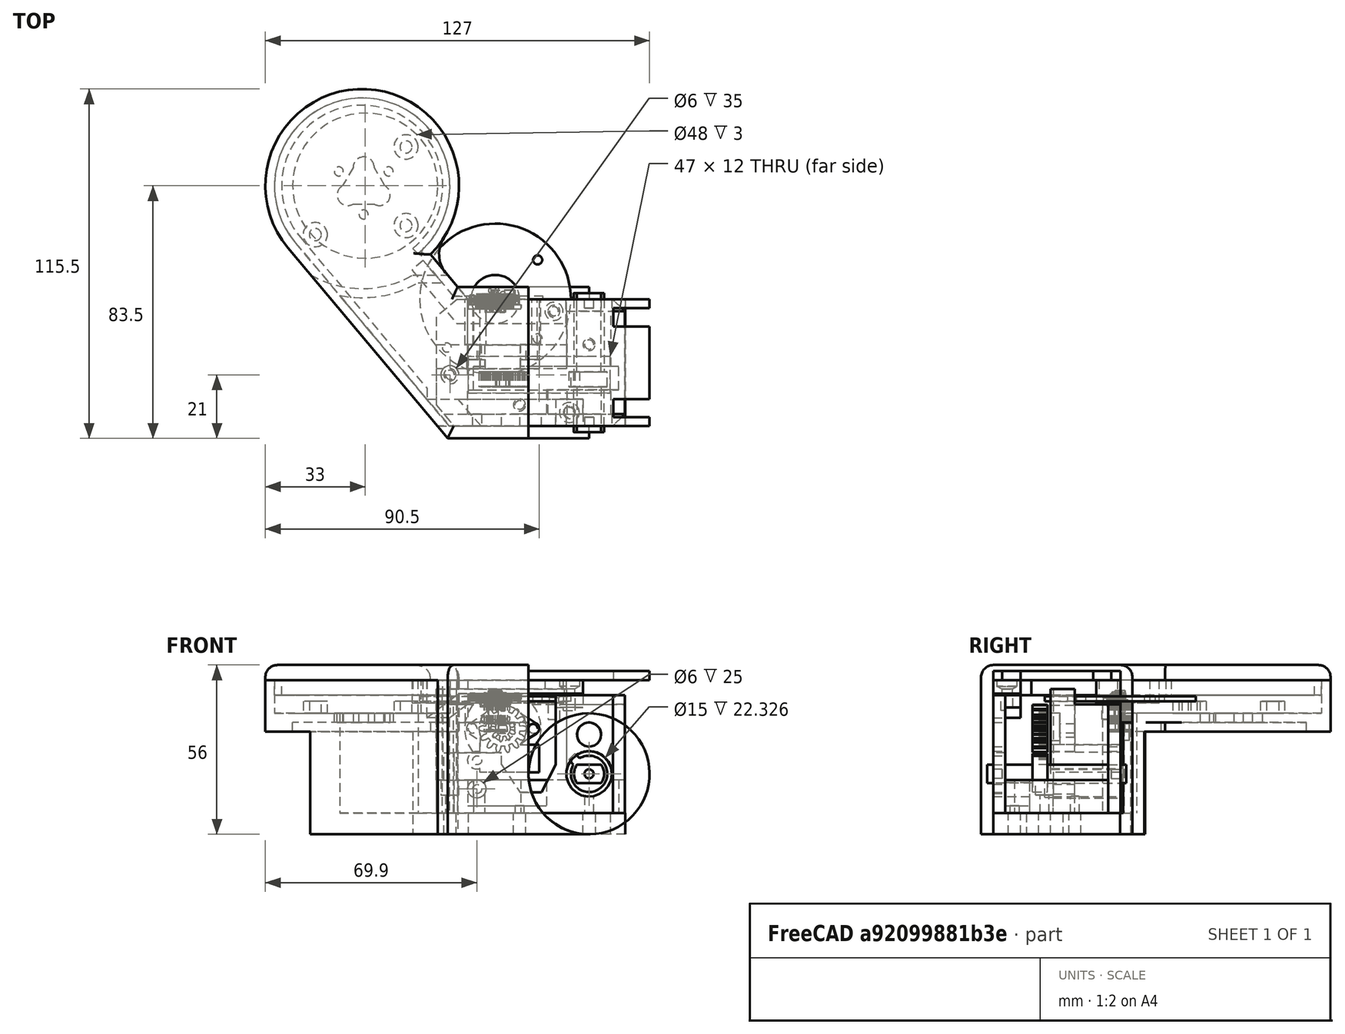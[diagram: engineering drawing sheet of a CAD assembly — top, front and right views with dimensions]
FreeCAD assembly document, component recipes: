
FREECAD ASSEMBLY — COMPONENT RECIPES ("ThirdArm")

This assembly document has 11 components, labeled P0..P10 below (a component is one placed body or linked part). 8 of them carry a construction recipe — the FreeCAD feature program that regenerates the part from scratch, quoted from this document or its linked companion documents; the rest are supplied as boundary geometry only. No exploded tour is included for this assembly.
COMPONENT P0 — recipe-attached ("SmallGear", modeled in this document).
Construction recipe (the document's own serialized feature program — sketch geometry with constraints, then the solid features built on it; lengths are millimeters unless a unit is written):

FEATURE [PartDesign::FeaturePython] InvoluteGear  label="InvoluteGear001"  # WARN: FeaturePython — macro-defined, semantics opaque (R4)
  AttacherType = Attacher::AttachEngine3D
  Suppressed = false
  addendum_diameter = 16
  angular_backlash = 0
  axle_hole = false
  axle_holesize = 10
  backlash = 0
  clearance = 0.25
  double_helix = false
  head = 0
  head_fillet = 0
  height = 5
  helix_angle = 0
  module = 1
  num_teeth = 14
  numpoints = 20
  offset_hole = false
  offset_holeoffset = 10
  offset_holesize = 10
  pitch_diameter = 14
  pressure_angle = 20
  properties_from_tool = false
  reversed_backlash = false
  root_diameter = 11.5
  root_fillet = 0
  shift = 0
  simple = false
  transverse_pitch = 3.14159
  traverse_module = 1
  undercut = false
  version = 1.3.0
  expr: angular_backlash = backlash / pitch_diameter * 360 ° / pi
FEATURE [Sketcher::SketchObject] Sketch002
  ArcFitTolerance = 1e-06
  AttachmentSupport = -> [InvoluteGear]
  FullyConstrained = false
  MakeInternals = false
  MapMode = 5
  Placement = pos=(0,0,5) rot=(0,0,1;0rad)
  sketch-geometry (5):
    g0: ArcOfCircle CenterX=0 CenterY=0 CenterZ=0 NormalX=0 NormalY=0 NormalZ=1 AngleXU=0 Radius=2.5 StartAngle=2.49809 EndAngle=3.78509
    g1: LineSegment StartX=2 StartY=1.5 StartZ=0 EndX=-2 EndY=1.5 EndZ=0
    g2: LineSegment StartX=-2 StartY=-1.5 StartZ=0 EndX=2 EndY=-1.5 EndZ=0
    g3: GeomPoint [constr] X=0 Y=0 Z=0
    g4: ArcOfCircle CenterX=0 CenterY=0 CenterZ=0 NormalX=0 NormalY=0 NormalZ=1 AngleXU=0 Radius=2.5 StartAngle=5.63968 EndAngle=6.92669
  constraints (10):
    c: Coincident(g0,g-1)
    c: Horizontal(g1)
    c: Horizontal(g2)
    c: Coincident(g3,g0)
    c: Equal(g0,g4)
    c: Coincident(g0,g4)
    c: Coincident(g2,g4)
    c: Coincident(g1,g4)
    c: Coincident(g1,g0)
    c: Coincident(g2,g0)
FEATURE [PartDesign::Pocket] Pocket001
  BaseFeature = -> InvoluteGear
  Direction = (0,0,-1)
  Length = 5
  Length2 = 5
  Profile = -> Sketch002
  ReferenceAxis = -> Sketch002 [N_Axis]
  Refine = true
  Suppressed = false
  Type = 1
FEATURE [PartDesign::Body] Body001  label="SmallGear"
  AllowCompound = false
  Group = -> [InvoluteGear,Sketch002,Pocket001]
  Origin = -> Origin002
  Placement = pos=(2.5,-24,-9) rot=(1,0,0;1.5708rad)
  Tip = -> Pocket001
COMPONENT P1 — recipe-attached ("ThirdArmHolder", modeled in this document).
Construction recipe (the document's own serialized feature program — sketch geometry with constraints, then the solid features built on it; lengths are millimeters unless a unit is written):

FEATURE [Sketcher::SketchObject] Sketch017
  ArcFitTolerance = 1e-06
  AttachmentSupport = -> [XY_Plane]
  FullyConstrained = false
  MakeInternals = false
  MapMode = 5
  sketch-geometry (4):
    g0: ArcOfCircle CenterX=-42 CenterY=37.5 CenterZ=0 NormalX=0 NormalY=0 NormalZ=1 AngleXU=0 Radius=32 StartAngle=5.49263 EndAngle=10.1229
    g1: LineSegment StartX=-66.5129 StartY=16.9302 StartZ=0 EndX=-6.82135 EndY=-54.2074 EndZ=0
    g2: LineSegment StartX=-19.4896 StartY=14.7562 StartZ=0 EndX=-6.82135 EndY=-0.341297 EndZ=0
    g3: LineSegment StartX=-6.82135 StartY=-0.341297 StartZ=0 EndX=-6.82135 EndY=-54.2074 EndZ=0
  constraints (10):
    c: Angle(g1,g-1) = 0.872665
    c: Angle(g-1,g2) = -0.872665
    c: Coincident(g3,g1)
    c: Vertical(g3)
    c: Coincident(g0,g1)
    c: Coincident(g0,g2)
    c: DistanceX(g0,g-1) = 42
    c: DistanceY(g-1,g0) = 37.5
    c: Radius(g0) = 32
    c: Coincident(g2,g3)
FEATURE [PartDesign::Pad] Pad010
  Direction = (0,0,1)
  Length = 14
  Length2 = 10
  Profile = -> Sketch017
  ReferenceAxis = -> Sketch017 [N_Axis]
  Refine = true
  Suppressed = false
  Type = 0
FEATURE [Sketcher::SketchObject] Sketch018
  ArcFitTolerance = 1e-06
  AttachmentSupport = -> [Pad010]
  ExternalGeometry = -> [Sketch017,Pad010]
  FullyConstrained = false
  MakeInternals = false
  MapMode = 5
  Placement = pos=(0,0,0) rot=(1,0,0;3.14159rad)
  sketch-geometry (8):
    g0: ArcOfCircle CenterX=-42 CenterY=-37.5 CenterZ=0 NormalX=0 NormalY=0 NormalZ=1 AngleXU=0 Radius=34 StartAngle=1.05435 EndAngle=2.09876
    g1: LineSegment StartX=-25.2111 StartY=-7.93429 StartZ=0 EndX=-13.7654 EndY=-7.93429 EndZ=0
    g2: LineSegment StartX=-13.7654 StartY=-7.93429 StartZ=0 EndX=-10.4314 EndY=-3.961 EndZ=0
    g3: LineSegment StartX=-59.1284 StartY=-8.12962 StartZ=0 EndX=-6.82135 EndY=54.2074 EndZ=0
    g4: GeomPoint X=-6.82135 Y=54.2074 Z=0
    g5: LineSegment StartX=-6.82135 StartY=54.2074 StartZ=0 EndX=45 EndY=54.2074 EndZ=0
    g6: LineSegment StartX=45 StartY=54.2074 StartZ=0 EndX=45 EndY=-3.961 EndZ=0
    g7: LineSegment StartX=45 StartY=-3.961 StartZ=0 EndX=-10.4314 EndY=-3.961 EndZ=0
  constraints (21):
    c: DistanceY(g0,g-1) = 37.5
    c: Coincident(g1,g0)
    c: Radius(g0) = 34
    c: Angle(g-1,g2) = 0.872665
    c: Coincident(g1,g2)
    c: Coincident(g0,g3)
    c: Angle(g-4) = 0.872665
    c: Angle(g-1,g3) = 0.872665
    c: Horizontal(g5)
    c: Coincident(g5,g3)
    c: Vertical(g6)
    c: Coincident(g6,g5)
    c: Horizontal(g7)
    c: Coincident(g3,g4)
    c: Coincident(g3,g-4)
    c: Coincident(g6,g7)
    c: Coincident(g2,g7)
    c: Horizontal(g1,g0)
    c: DistanceX(g0,g-1) = 42
    c: Block(g1)
    c: Distance(g-2,g6) = 45
FEATURE [PartDesign::Thickness] Thickness
  Base = -> Pad010 [Face6]
  BaseFeature = -> Pad010
  Intersection = true
  Join = 0
  Mode = 0
  Refine = true
  Reversed = true
  SupportTransform = false
  Suppressed = false
  Value = 3
FEATURE [PartDesign::Pad] Pad011
  BaseFeature = -> Thickness
  Direction = (0,0,-1)
  Length = 37
  Length2 = 10
  Profile = -> Sketch018
  ReferenceAxis = -> Sketch018 [N_Axis]
  Refine = true
  Suppressed = false
  Type = 0
FEATURE [Sketcher::SketchObject] Sketch019
  ArcFitTolerance = 1e-06
  AttachmentSupport = -> [Pad011]
  ExternalGeometry = -> [Pad011]
  FullyConstrained = false
  MakeInternals = false
  MapMode = 5
  Placement = pos=(0,0,14) rot=(0,0,1;0rad)
  sketch-geometry (10):
    g0: LineSegment StartX=-17.5 StartY=-62.76 StartZ=0 EndX=50.544 EndY=-62.76 EndZ=0
    g1: LineSegment StartX=50.544 StartY=-62.76 StartZ=0 EndX=50.544 EndY=0.961001 EndZ=0
    g2: LineSegment StartX=50.544 StartY=0.961001 StartZ=0 EndX=-17.0127 EndY=0.961001 EndZ=0
    g3: LineSegment StartX=-32.1829 StartY=-42 StartZ=0 EndX=-32.1829 EndY=-55.0243 EndZ=0
    g4: LineSegment StartX=-32.1829 StartY=-55.0243 StartZ=0 EndX=-17.5 EndY=-55.0243 EndZ=0
    g5: LineSegment StartX=-13.1484 StartY=-42 StartZ=0 EndX=-32.1829 EndY=-42 EndZ=0
    g6: LineSegment StartX=-17.5 StartY=-55.0243 StartZ=0 EndX=-17.5 EndY=-62.76 EndZ=0
    g7: LineSegment StartX=-19 StartY=-35.0263 StartZ=0 EndX=-13.1484 EndY=-42 EndZ=0
    g8: LineSegment StartX=-19 StartY=-35.0263 StartZ=0 EndX=-19 EndY=-1.02632 EndZ=0
    g9: LineSegment StartX=-19 StartY=-1.02632 StartZ=0 EndX=-17.0127 EndY=0.961001 EndZ=0
  constraints (24):
    c: Coincident(g0,g1)
    c: Coincident(g1,g2)
    c: Coincident(g6,g0)
    c: Horizontal(g0)
    c: Horizontal(g2)
    c: Vertical(g1)
    c: Distance(g-1,g0) = 62.76
    c: Coincident(g3,g4)
    c: Coincident(g5,g3)
    c: Vertical(g3)
    c: Horizontal(g4)
    c: Horizontal(g5)
    c: Coincident(g4,g6)
    c: Coincident(g7,g5)
    c: Distance(g-1,g5) = 42
    c: Coincident(g8,g7)
    c: Vertical(g8)
    c: Coincident(g9,g8)
    c: Coincident(g9,g2)
    c: Distance(g-2,g8) = 19
    c: Angle(g-1,g9) = 0.785398
    c: Angle(g7,g5) = 0.872665
    c: DistanceY(g8,g8) = 34
    c: Distance(g-4,g2) = 3
FEATURE [PartDesign::Pocket] Pocket007
  BaseFeature = -> Pad011
  Direction = (0,0,-1)
  Length = 44
  Length2 = 5
  Profile = -> Sketch019
  ReferenceAxis = -> Sketch019 [N_Axis]
  Refine = true
  Suppressed = false
  Type = 0
FEATURE [Sketcher::SketchObject] Sketch020
  ArcFitTolerance = 1e-06
  AttachmentSupport = -> [Pocket007]
  FullyConstrained = false
  MakeInternals = false
  MapMode = 5
  Placement = pos=(0,0,14) rot=(0,0,1;0rad)
  sketch-geometry (4):
    g0: LineSegment StartX=54.2024 StartY=-63.0343 StartZ=0 EndX=54.2024 EndY=-42 EndZ=0
    g1: LineSegment StartX=54.2024 StartY=-42 StartZ=0 EndX=-35.8003 EndY=-42 EndZ=0
    g2: LineSegment StartX=-35.8003 StartY=-42 StartZ=0 EndX=-35.8003 EndY=-63.0343 EndZ=0
    g3: LineSegment StartX=-35.8003 StartY=-63.0343 StartZ=0 EndX=54.2024 EndY=-63.0343 EndZ=0
  constraints (9):
    c: Coincident(g0,g1)
    c: Coincident(g1,g2)
    c: Coincident(g2,g3)
    c: Coincident(g3,g0)
    c: Vertical(g0)
    c: Vertical(g2)
    c: Horizontal(g1)
    c: Horizontal(g3)
    c: Distance(g-1,g1) = 42
FEATURE [PartDesign::Pocket] Pocket008
  BaseFeature = -> Pocket007
  Direction = (0,0,-1)
  Length = 5
  Length2 = 5
  Profile = -> Sketch020
  ReferenceAxis = -> Sketch020 [N_Axis]
  Refine = true
  Suppressed = false
  Type = 1
FEATURE [Sketcher::SketchObject] Sketch021
  ArcFitTolerance = 1e-06
  AttachmentSupport = -> [Pocket008]
  FullyConstrained = false
  MakeInternals = false
  MapMode = 5
  Placement = pos=(0,3.961,0) rot=(0,0.707107,0.707107;3.14159rad)
  sketch-geometry (5):
    g0: ArcOfCircle CenterX=-33 CenterY=-17 CenterZ=0 NormalX=0 NormalY=0 NormalZ=1 AngleXU=0 Radius=20 StartAngle=4.71239 EndAngle=6.28319
    g1: LineSegment StartX=-13 StartY=-17 StartZ=0 EndX=-13 EndY=6.96255 EndZ=0
    g2: LineSegment StartX=-13 StartY=6.96255 StartZ=0 EndX=-66.8614 EndY=6.96255 EndZ=0
    g3: LineSegment StartX=-66.8614 StartY=6.96255 StartZ=0 EndX=-66.8614 EndY=-37 EndZ=0
    g4: LineSegment StartX=-66.8614 StartY=-37 StartZ=0 EndX=-33.0001 EndY=-37 EndZ=0
  constraints (14):
    c: Radius(g0) = 20
    c: Distance(g0,g-1) = 17
    c: Vertical(g1)
    c: Coincident(g1,g0)
    c: Horizontal(g2)
    c: Coincident(g2,g1)
    c: Coincident(g0,g4)
    c: Coincident(g3,g4)
    c: Coincident(g2,g3)
    c: Horizontal(g0,g0)
    c: Horizontal(g4)
    c: Distance(g0,g-2) = 33
    c: Vertical(g3)
    c: Distance(g0,g4) = 20
FEATURE [PartDesign::Pocket] Pocket009
  BaseFeature = -> Pocket008
  Direction = (0,-1,2e-16)
  Length = 4
  Length2 = 5
  Profile = -> Sketch021
  ReferenceAxis = -> Sketch021 [N_Axis]
  Refine = true
  Suppressed = false
  Type = 0
FEATURE [Sketcher::SketchObject] Sketch031
  ArcFitTolerance = 1e-06
  AttachmentSupport = -> [Thickness]
  FullyConstrained = false
  MakeInternals = false
  MapMode = 5
  Placement = pos=(0,0,3) rot=(0,0,1;0rad)
  sketch-geometry (11):
    g0: GeomPoint [constr] X=-41.5 Y=37.5 Z=0
    g1: LineSegment StartX=-34.5 StartY=37.5 StartZ=0 EndX=-38 EndY=43.5622 EndZ=0
    g2: Circle [constr] CenterX=-41.5 CenterY=37.5 CenterZ=0 NormalX=0 NormalY=0 NormalZ=1 AngleXU=0 Radius=7
    g3: ArcOfCircle CenterX=-41.5 CenterY=43.5368 CenterZ=0 NormalX=0 NormalY=0 NormalZ=1 AngleXU=0 Radius=3.50009 StartAngle=0.00725319 EndAngle=3.13434
    g4: ArcOfCircle CenterX=-36.2363 CenterY=34.461 CenterZ=0 NormalX=0 NormalY=0 NormalZ=1 AngleXU=0 Radius=3.50004 StartAngle=4.18428 EndAngle=7.3349
    g5: ArcOfCircle CenterX=-46.7609 CenterY=34.4626 CenterZ=0 NormalX=0 NormalY=0 NormalZ=1 AngleXU=0 Radius=3.50002 StartAngle=2.0908 EndAngle=5.23958
    g6: LineSegment StartX=-45 StartY=43.5622 StartZ=0 EndX=-48.5 EndY=37.5 EndZ=0
    g7: LineSegment StartX=-45 StartY=31.4378 StartZ=0 EndX=-38 EndY=31.4378 EndZ=0
    g8: Circle CenterX=-41.5 CenterY=28 CenterZ=0 NormalX=0 NormalY=0 NormalZ=1 AngleXU=0 Radius=1.5
    g9: Circle CenterX=-33.2728 CenterY=42.25 CenterZ=0 NormalX=0 NormalY=0 NormalZ=1 AngleXU=0 Radius=1.5
    g10: Circle CenterX=-49.7272 CenterY=42.25 CenterZ=0 NormalX=0 NormalY=0 NormalZ=1 AngleXU=0 Radius=1.5
  constraints (24):
    c: DistanceX(g0,g-1) = 41.5
    c: DistanceY(g-1,g0) = 37.5
    c: PointOnObject(g1,g2)
    c: PointOnObject(g5,g2)
    c: PointOnObject(g4,g2)
    c: PointOnObject(g1,g2)
    c: Radius(g2) = 7
    c: Coincident(g2,g0)
    c: Coincident(g3,g1)
    c: Coincident(g4,g1)
    c: Coincident(g6,g3)
    c: Coincident(g6,g5)
    c: Coincident(g7,g5)
    c: Coincident(g7,g4)
    c: Horizontal(g7)
    c: Diameter(g8) = 3
    c: DistanceY(g8,g0) = 9.5
    c: Vertical(g0,g8)
    c: Diameter(g9) = 3
    c: Distance(g9,g0) = 9.5
    c: DistanceY(g0,g9) = 4.75
    c: Diameter(g10) = 3
    c: Distance(g10,g0) = 9.5
    c: DistanceY(g0,g10) = 4.75
FEATURE [PartDesign::Pocket] Pocket028
  BaseFeature = -> Pocket009
  Direction = (0,0,-1)
  Length = 5
  Length2 = 5
  Profile = -> Sketch031
  ReferenceAxis = -> Sketch031 [N_Axis]
  Refine = true
  Suppressed = false
  Type = 0
FEATURE [PartDesign::Fillet] Fillet006
  Base = -> Pocket028 [Edge1]
  BaseFeature = -> Pocket028
  Radius = 10
  Refine = true
  SupportTransform = false
  Suppressed = false
  UseAllEdges = false
FEATURE [Sketcher::SketchObject] Sketch052
  ArcFitTolerance = 1e-06
  FullyConstrained = false
  MakeInternals = false
  MapMode = 5
  Placement = pos=(0,0,0) rot=(1,0,0;3.14159rad)
  sketch-geometry (6):
    g0: ArcOfCircle CenterX=-42 CenterY=-37.5 CenterZ=0 NormalX=0 NormalY=0 NormalZ=1 AngleXU=0 Radius=32 StartAngle=2.44344 EndAngle=7.07374
    g1: ArcOfCircle CenterX=-42 CenterY=-37.5 CenterZ=0 NormalX=0 NormalY=0 NormalZ=1 AngleXU=0 Radius=34 StartAngle=1.05435 EndAngle=2.09876
    g2: LineSegment StartX=-59.1284 StartY=-8.12962 StartZ=0 EndX=-66.5129 EndY=-16.9302 EndZ=0
    g3: LineSegment StartX=-13.7654 StartY=-7.93429 StartZ=0 EndX=-25.2111 EndY=-7.93429 EndZ=0
    g4: LineSegment StartX=-13.7654 StartY=-7.93429 StartZ=0 EndX=-19.4896 EndY=-14.7562 EndZ=0
    g5: Circle CenterX=-41 CenterY=-37.5 CenterZ=0 NormalX=0 NormalY=0 NormalZ=1 AngleXU=0 Radius=24
  constraints (13):
    c: Coincident(g0,g-6)
    c: Coincident(g0,g-7)
    c: Coincident(g1,g0)
    c: Coincident(g1,g-6)
    c: Coincident(g2,g1)
    c: Coincident(g2,g0)
    c: Coincident(g3,g-5)
    c: Coincident(g3,g1)
    c: Coincident(g4,g3)
    c: Coincident(g4,g0)
    c: Diameter(g5) = 48
    c: Distance(g5,g-1) = 37.5
    c: Distance(g5,g-2) = 41
FEATURE [PartDesign::Pad] Pad021
  BaseFeature = -> Fillet006
  Direction = (0,-1e-16,-1)
  Length = 3
  Length2 = 10
  Profile = -> Sketch052
  ReferenceAxis = -> Sketch052 [N_Axis]
  Refine = true
  Suppressed = false
  Type = 0
FEATURE [Sketcher::SketchObject] Sketch053
  ArcFitTolerance = 1e-06
  AttachmentSupport = -> [Pocket028]
  ExternalGeometry = -> [Pocket028]
  FullyConstrained = false
  MakeInternals = false
  MapMode = 5
  Placement = pos=(0,0,3) rot=(0,0,1;0rad)
  sketch-geometry (7):
    g0: ArcOfCircle CenterX=-42 CenterY=37.5 CenterZ=0 NormalX=0 NormalY=0 NormalZ=1 AngleXU=0 Radius=37 StartAngle=4.50979 EndAngle=5.23479
    g1: LineSegment StartX=-23.5384 StartY=5.43491 StartZ=0 EndX=-15.5844 EndY=5.43491 EndZ=0
    g2: LineSegment StartX=-11.8303 StartY=0.961001 StartZ=0 EndX=-15.5844 EndY=5.43491 EndZ=0
    g3: LineSegment StartX=-11.8303 StartY=0.961001 StartZ=0 EndX=-17.0127 EndY=0.961001 EndZ=0
    g4: LineSegment StartX=-17.0127 StartY=0.961001 StartZ=0 EndX=-19 EndY=-1.0704 EndZ=0
    g5: LineSegment StartX=-19 StartY=-1.0704 StartZ=0 EndX=-19 EndY=-35.0263 EndZ=0
    g6: LineSegment StartX=-19 StartY=-35.0263 StartZ=0 EndX=-49.4452 EndY=1.2568 EndZ=0
  constraints (14):
    c: Radius(g0) = 37
    c: Horizontal(g1)
    c: Coincident(g1,g0)
    c: PointOnObject(g1,g-6)
    c: Coincident(g2,g-8)
    c: Coincident(g2,g1)
    c: Coincident(g3,g2)
    c: Coincident(g3,g-8)
    c: Coincident(g3,g4)
    c: Coincident(g4,g-9)
    c: Coincident(g4,g5)
    c: Coincident(g5,g-9)
    c: Coincident(g5,g6)
    c: Coincident(g6,g0)
FEATURE [PartDesign::Pocket] Pocket029
  BaseFeature = -> Pad021
  Direction = (0,0,-1)
  Length = 33
  Length2 = 5
  Profile = -> Sketch053
  ReferenceAxis = -> Sketch053 [N_Axis]
  Refine = true
  Suppressed = false
  Type = 0
FEATURE [Sketcher::SketchObject] Sketch054
  ArcFitTolerance = 1e-06
  AttachmentSupport = -> [Pocket029]
  FullyConstrained = true
  MakeInternals = false
  MapMode = 5
  Placement = pos=(0,0,-30) rot=(0,0,1;0rad)
  sketch-geometry (7):
    g0: Circle CenterX=-13 CenterY=-25 CenterZ=0 NormalX=0 NormalY=0 NormalZ=1 AngleXU=0 Radius=2
    g1: Circle CenterX=33 CenterY=-15 CenterZ=0 NormalX=0 NormalY=0 NormalZ=1 AngleXU=0 Radius=2
    g2: LineSegment StartX=-7 StartY=-19 StartZ=0 EndX=-7 EndY=-31 EndZ=0
    g3: LineSegment StartX=-7 StartY=-31 StartZ=0 EndX=40 EndY=-31 EndZ=0
    g4: LineSegment StartX=40 StartY=-31 StartZ=0 EndX=40 EndY=-19 EndZ=0
    g5: LineSegment StartX=40 StartY=-19 StartZ=0 EndX=-7 EndY=-19 EndZ=0
    g6: Circle CenterX=10 CenterY=-35 CenterZ=0 NormalX=0 NormalY=0 NormalZ=1 AngleXU=0 Radius=2
  constraints (21):
    c: Diameter(g0) = 4
    c: Diameter(g1) = 4
    c: DistanceY(g1,g-1) = 15
    c: Distance(g1,g-2) = 33
    c: DistanceX(g0,g-1) = 13
    c: DistanceY(g0,g-1) = 25
    c: Coincident(g2,g3)
    c: Coincident(g3,g4)
    c: Coincident(g4,g5)
    c: Coincident(g5,g2)
    c: Vertical(g2)
    c: Vertical(g4)
    c: Horizontal(g3)
    c: Horizontal(g5)
    c: DistanceY(g4,g4) = 12
    c: DistanceX(g3,g3) = 47
    c: DistanceY(g4,g-1) = 19
    c: DistanceX(g-1,g4) = 40
    c: Diameter(g6) = 4
    c: DistanceX(g-1,g6) = 10
    c: DistanceY(g6,g-1) = 35
FEATURE [PartDesign::Pocket] Pocket030
  BaseFeature = -> Pocket029
  Direction = (0,0,-1)
  Length = 5
  Length2 = 5
  Profile = -> Sketch054
  ReferenceAxis = -> Sketch054 [N_Axis]
  Refine = true
  Suppressed = false
  Type = 1
FEATURE [Sketcher::SketchObject] Sketch057
  ArcFitTolerance = 1e-06
  AttachmentSupport = -> [Pocket030]
  FullyConstrained = true
  MakeInternals = false
  MapMode = 5
  Placement = pos=(0,0.961001,0) rot=(1,0,0;1.5708rad)
  sketch-geometry (1):
    g0: Circle CenterX=4.5 CenterY=-2 CenterZ=0 NormalX=0 NormalY=0 NormalZ=1 AngleXU=0 Radius=4
  constraints (3):
    c: Diameter(g0) = 8
    c: DistanceX(g-1,g0) = 4.5
    c: DistanceY(g0,g-1) = 2
FEATURE [PartDesign::Pocket] Pocket033
  BaseFeature = -> Pocket030
  Direction = (0,1,-2e-16)
  Length = 2
  Length2 = 5
  Profile = -> Sketch057
  ReferenceAxis = -> Sketch057 [N_Axis]
  Refine = true
  Suppressed = false
  Type = 0
FEATURE [Sketcher::SketchObject] Sketch058
  ArcFitTolerance = 1e-06
  AttachmentSupport = -> [Pocket033]
  ExternalGeometry = -> [Pocket033]
  FullyConstrained = true
  MakeInternals = false
  MapMode = 5
  Placement = pos=(0,0,14) rot=(0,0,1;0rad)
  sketch-geometry (4):
    g0: LineSegment StartX=-13.1484 StartY=-42 StartZ=0 EndX=-20.7003 EndY=-33 EndZ=0
    g1: LineSegment StartX=-20.7003 StartY=-33 StartZ=0 EndX=31 EndY=-33 EndZ=0
    g2: LineSegment StartX=31 StartY=-33 StartZ=0 EndX=31 EndY=-42 EndZ=0
    g3: LineSegment StartX=31 StartY=-42 StartZ=0 EndX=-13.1484 EndY=-42 EndZ=0
  constraints (11):
    c: Coincident(g-3,g0)
    c: PointOnObject(g0,g-3)
    c: Coincident(g0,g1)
    c: Horizontal(g1)
    c: Coincident(g1,g2)
    c: Vertical(g2)
    c: Coincident(g2,g3)
    c: Coincident(g3,g0)
    c: Horizontal(g3)
    c: Distance(g-2,g2) = 31
    c: DistanceY(g2,g2) = 9
FEATURE [PartDesign::Pad] Pad022
  BaseFeature = -> Pocket033
  Direction = (0,0,1)
  Length = 4.5
  Length2 = 10
  Profile = -> Sketch058
  ReferenceAxis = -> Sketch058 [N_Axis]
  Refine = true
  Reversed = true
  Suppressed = false
  Type = 0
FEATURE [Sketcher::SketchObject] Sketch061
  ArcFitTolerance = 1e-06
  AttachmentSupport = -> [Pad022]
  FullyConstrained = true
  MakeInternals = false
  MapMode = 5
  Placement = pos=(0,0,14) rot=(0,0,1;0rad)
  sketch-geometry (1):
    g0: Circle CenterX=26.5 CenterY=-37.5 CenterZ=0 NormalX=0 NormalY=0 NormalZ=1 AngleXU=0 Radius=1.5
  constraints (3):
    c: Diameter(g0) = 3
    c: DistanceX(g-1,g0) = 26.5
    c: DistanceY(g0,g-1) = 37.5
FEATURE [PartDesign::Hole] Hole
  BaseFeature = -> Pad022
  CustomThreadClearance = 0
  Depth = 6
  DepthType = 0
  Diameter = 3.4
  DrillForDepth = false
  DrillPoint = 0
  DrillPointAngle = 118
  HoleCutCountersinkAngle = 90
  HoleCutCustomValues = false
  HoleCutDepth = 0
  HoleCutDiameter = 6.1
  HoleCutType = 0
  ModelThread = false
  Profile = -> Sketch061
  Refine = true
  Suppressed = false
  Tapered = false
  TaperedAngle = 90
  ThreadClass = 0
  ThreadDepth = 6
  ThreadDepthType = 0
  ThreadDirection = 0
  ThreadFit = 0
  ThreadSize = 9
  ThreadType = 1
  Threaded = false
  UseCustomThreadClearance = false
FEATURE [PartDesign::Hole] Hole001
  BaseFeature = -> Hole
  CustomThreadClearance = 0
  Depth = 2
  DepthType = 0
  Diameter = 6.6
  DrillForDepth = false
  DrillPoint = 1
  DrillPointAngle = 118
  HoleCutCountersinkAngle = 90
  HoleCutCustomValues = false
  HoleCutDepth = 0
  HoleCutDiameter = 0
  HoleCutType = 0
  ModelThread = false
  Profile = -> Sketch061
  Refine = true
  Suppressed = false
  Tapered = false
  TaperedAngle = 90
  ThreadClass = 0
  ThreadDepth = 2
  ThreadDepthType = 0
  ThreadDirection = 0
  ThreadFit = 0
  ThreadSize = 14
  ThreadType = 1
  Threaded = false
  UseCustomThreadClearance = false
FEATURE [PartDesign::Chamfer] Chamfer
  Angle = 45
  Base = -> Hole001 [Edge87]
  BaseFeature = -> Hole001
  ChamferType = 0
  FlipDirection = false
  Refine = true
  Size = 8
  Size2 = 1
  SupportTransform = false
  Suppressed = false
  UseAllEdges = false
FEATURE [Sketcher::SketchObject] Sketch062
  ArcFitTolerance = 1e-06
  AttachmentSupport = -> [Chamfer]
  ExternalGeometry = -> [Chamfer]
  FullyConstrained = false
  MakeInternals = false
  MapMode = 5
  Placement = pos=(0,0,14) rot=(0,0,1;0rad)
  sketch-geometry (8):
    g0: LineSegment StartX=-21.7877 StartY=12.8278 StartZ=0 EndX=-25.5719 EndY=9.6525 EndZ=0
    g1: LineSegment StartX=-25.5719 StartY=9.6525 StartZ=0 EndX=-10.7597 EndY=-8 EndZ=0
    g2: LineSegment StartX=-10.7597 StartY=-8 StartZ=0 EndX=25.4051 EndY=-8 EndZ=0
    g3: LineSegment StartX=25.4051 StartY=-8 StartZ=0 EndX=25.4051 EndY=0 EndZ=0
    g4: LineSegment StartX=-11.8303 StartY=0.961001 StartZ=0 EndX=-21.7877 EndY=12.8278 EndZ=0
    g5: LineSegment StartX=-11.8303 StartY=0.961001 StartZ=0 EndX=-7.9141 EndY=0.961001 EndZ=0
    g6: LineSegment StartX=-7.9141 StartY=0.961001 StartZ=0 EndX=-7.10773 EndY=1e-16 EndZ=0
    g7: LineSegment StartX=-7.10773 StartY=1e-16 StartZ=0 EndX=25.4051 EndY=1e-16 EndZ=0
  constraints (20):
    c: Coincident(g0,g1)
    c: Coincident(g1,g2)
    c: Horizontal(g2)
    c: Coincident(g2,g3)
    c: Coincident(g4,g0)
    c: Vertical(g3)
    c: Distance(g3,g3) = 8
    c: Angle(g4,g0) = 1.5708
    c: Angle(g1,g0) = 1.5708
    c: Coincident(g0,g-3)
    c: Angle(g4,g-1) = 0.872665
    c: PointOnObject(g4,g-4)
    c: Coincident(g4,g5)
    c: Coincident(g5,g-4)
    c: Coincident(g5,g6)
    c: PointOnObject(g6,g-1)
    c: Coincident(g6,g7)
    c: Coincident(g7,g3)
    c: Horizontal(g7)
    c: Angle(g7,g6) = 2.26893
FEATURE [PartDesign::Pad] Pad023
  BaseFeature = -> Chamfer
  Direction = (0,0,1)
  Length = 7.5
  Length2 = 10
  Profile = -> Sketch062
  ReferenceAxis = -> Sketch062 [N_Axis]
  Refine = true
  Reversed = true
  Suppressed = false
  Type = 0
FEATURE [Sketcher::SketchObject] Sketch063
  ArcFitTolerance = 1e-06
  AttachmentSupport = -> [Pad023]
  ExternalGeometry = -> [Pad023]
  FullyConstrained = true
  MakeInternals = false
  MapMode = 5
  Placement = pos=(0,0,14) rot=(0,0,1;0rad)
  sketch-geometry (1):
    g0: Circle CenterX=21.4051 CenterY=-4 CenterZ=0 NormalX=0 NormalY=0 NormalZ=1 AngleXU=0 Radius=1.5
  constraints (3):
    c: Diameter(g0) = 3
    c: Distance(g0,g-3) = 4
    c: DistanceY(g-3,g0) = 4
FEATURE [PartDesign::Hole] Hole002
  BaseFeature = -> Pad023
  CustomThreadClearance = 0
  Depth = 5
  DepthType = 0
  Diameter = 6
  DrillForDepth = false
  DrillPoint = 1
  DrillPointAngle = 118
  HoleCutCountersinkAngle = 90
  HoleCutCustomValues = false
  HoleCutDepth = 0
  HoleCutDiameter = 6.1
  HoleCutType = 0
  ModelThread = false
  Profile = -> Sketch063
  Refine = true
  Suppressed = false
  Tapered = false
  TaperedAngle = 90
  ThreadClass = 0
  ThreadDepth = 5
  ThreadDepthType = 0
  ThreadDirection = 0
  ThreadFit = 0
  ThreadSize = 0
  ThreadType = 0
  Threaded = false
  UseCustomThreadClearance = false
FEATURE [PartDesign::Pocket] Pocket035
  BaseFeature = -> Hole002
  Direction = (0,0,-1)
  Length = 8
  Length2 = 5
  Profile = -> Sketch063
  ReferenceAxis = -> Sketch063 [N_Axis]
  Refine = true
  Suppressed = false
  Type = 0
FEATURE [Sketcher::SketchObject] Sketch065
  ArcFitTolerance = 1e-06
  AttachmentSupport = -> [Pocket035]
  FullyConstrained = false
  MakeInternals = false
  MapMode = 5
  Placement = pos=(0,0,3) rot=(0,0,1;0rad)
  sketch-geometry (6):
    g0: Circle CenterX=-27.5 CenterY=50.3515 CenterZ=0 NormalX=0 NormalY=0 NormalZ=1 AngleXU=0 Radius=4
    g1: Circle CenterX=-27.5 CenterY=24.3515 CenterZ=0 NormalX=0 NormalY=0 NormalZ=1 AngleXU=0 Radius=4
    g2: Circle CenterX=-57.5 CenterY=21.3515 CenterZ=0 NormalX=0 NormalY=0 NormalZ=1 AngleXU=0 Radius=4
    g3: Circle CenterX=-27.5 CenterY=50.3515 CenterZ=0 NormalX=0 NormalY=0 NormalZ=1 AngleXU=0 Radius=2
    g4: Circle CenterX=-27.5 CenterY=24.3515 CenterZ=0 NormalX=0 NormalY=0 NormalZ=1 AngleXU=0 Radius=2
    g5: Circle CenterX=-57.5 CenterY=21.3515 CenterZ=0 NormalX=0 NormalY=0 NormalZ=1 AngleXU=0 Radius=2
  constraints (14):
    c: Diameter(g0) = 8
    c: Diameter(g1) = 8
    c: Vertical(g1,g0)
    c: DistanceX(g1,g-1) = 27.5
    c: Diameter(g2) = 8
    c: DistanceX(g2,g1) = 30
    c: DistanceY(g2,g1) = 3
    c: DistanceY(g1,g0) = 26
    c: Diameter(g3) = 4
    c: Coincident(g3,g0)
    c: Diameter(g4) = 4
    c: Coincident(g4,g1)
    c: Diameter(g5) = 4
    c: Coincident(g5,g2)
FEATURE [PartDesign::Pad] Pad024
  BaseFeature = -> Pocket035
  Direction = (0,0,1)
  Length = 4
  Length2 = 10
  Profile = -> Sketch065
  ReferenceAxis = -> Sketch065 [N_Axis]
  Refine = true
  Suppressed = false
  Type = 0
FEATURE [Sketcher::SketchObject] Sketch067
  ArcFitTolerance = 1e-06
  AttachmentSupport = -> [Pad024]
  ExternalGeometry = -> [Pad024]
  FullyConstrained = false
  MakeInternals = false
  MapMode = 5
  Placement = pos=(0,0,3) rot=(0,0,1;0rad)
  sketch-geometry (8):
    g0: LineSegment StartX=-41 StartY=37.5 StartZ=0 EndX=6.96769 EndY=-19.6657 EndZ=0
    g1: LineSegment StartX=6.96769 StartY=-42 StartZ=0 EndX=6.96769 EndY=0 EndZ=0
    g2: LineSegment StartX=6.96769 StartY=-19.6657 StartZ=0 EndX=33 EndY=-19.6657 EndZ=0
    g3: LineSegment StartX=33 StartY=-19.6657 StartZ=0 EndX=33 EndY=-16.3056 EndZ=0
    g4: LineSegment StartX=33 StartY=-16.3056 StartZ=0 EndX=29 EndY=-16.3056 EndZ=0
    g5: LineSegment StartX=33 StartY=-16.3056 StartZ=0 EndX=37 EndY=-16.3056 EndZ=0
    g6: LineSegment StartX=33 StartY=-19.6657 StartZ=0 EndX=153.063 EndY=-19.6657 EndZ=0
    g7: LineSegment StartX=153.063 StartY=-19.6657 StartZ=0 EndX=153.063 EndY=2.01091 EndZ=0
  constraints (20):
    c: Angle(g-1,g0) = -0.872665
    c: Coincident(g0,g-3)
    c: Symmetric(g-4,g-4,g1)
    c: PointOnObject(g1,g-5)
    c: Vertical(g1)
    c: PointOnObject(g0,g1)
    c: Coincident(g0,g2)
    c: Horizontal(g2)
    c: Vertical(g3)
    c: Coincident(g3,g2)
    c: Coincident(g3,g4)
    c: Coincident(g3,g5)
    c: Symmetric(g4,g5,g3)
    c: Horizontal(g4)
    c: DistanceX(g-1,g4) = 29
    c: DistanceX(g4,g5) = 8
    c: Coincident(g2,g6)
    c: Horizontal(g6)
    c: Coincident(g6,g7)
    c: Vertical(g7)
FEATURE [PartDesign::Body] Body004  label="ThirdArmHolder"
  AllowCompound = false
  Group = -> [Sketch017,Pad010,Thickness,Sketch018,Pad011,Sketch019,Pocket007,Sketch020,Pocket008,Sketch021,Pocket009,Sketch031,Pocket028,Fillet006,Sketch052,Pad021,Sketch053,Pocket029,Sketch054,Pocket030,Sketch057,Pocket033,Sketch058,Pad022,Sketch061,Hole,Hole001,Chamfer,Sketch062,Pad023,Sketch063,Hole002,Pocket035,Sketch065,Pad024,Sketch067]
  Origin = -> Origin
  Placement = pos=(-2,0,-7) rot=(0,0,1;0rad)
  Tip = -> Pad024
COMPONENT P2 — recipe-attached ("ThirdArmLid", modeled in this document).
Construction recipe (the document's own serialized feature program — sketch geometry with constraints, then the solid features built on it; lengths are millimeters unless a unit is written):

FEATURE [Sketcher::SketchObject] Sketch025
  ArcFitTolerance = 1e-06
  AttachmentSupport = -> [XY_Plane005]
  FullyConstrained = false
  MakeInternals = false
  MapMode = 5
  sketch-geometry (6):
    g0: ArcOfCircle CenterX=-42 CenterY=37.5 CenterZ=0 NormalX=0 NormalY=0 NormalZ=1 AngleXU=0 Radius=32 StartAngle=5.49278 EndAngle=10.1229
    g1: LineSegment StartX=-66.5134 StartY=16.9308 StartZ=0 EndX=-13.7082 EndY=-46 EndZ=0
    g2: LineSegment StartX=-19.4862 StartY=14.7596 StartZ=0 EndX=-10.4578 EndY=4 EndZ=0
    g3: LineSegment StartX=-13.7082 StartY=-46 StartZ=0 EndX=13 EndY=-46 EndZ=0
    g4: LineSegment StartX=-10.4578 StartY=4 StartZ=0 EndX=13 EndY=4 EndZ=0
    g5: LineSegment StartX=13 StartY=-46 StartZ=0 EndX=13 EndY=4 EndZ=0
  constraints (18):
    c: Angle(g1,g-1) = 0.872665
    c: Angle(g-1,g2) = -0.872665
    c: Coincident(g0,g1)
    c: Coincident(g0,g2)
    c: DistanceX(g0,g-1) = 42
    c: DistanceY(g-1,g0) = 37.5
    c: Radius(g0) = 32
    c: Distance(g-1,g2) = 5.44
    c: Horizontal(g3)
    c: Coincident(g3,g1)
    c: Horizontal(g4)
    c: Coincident(g4,g2)
    c: Vertical(g5)
    c: Coincident(g3,g5)
    c: Coincident(g4,g5)
    c: Distance(g-1,g3) = 46
    c: Distance(g-1,g4) = 4
    c: Distance(g-2,g5) = 13
FEATURE [PartDesign::Pad] Pad012  label="Pad00"
  Direction = (0,0,1)
  Length = 5
  Length2 = 10
  Profile = -> Sketch025
  ReferenceAxis = -> Sketch025 [N_Axis]
  Refine = true
  Suppressed = false
  Type = 0
FEATURE [Sketcher::SketchObject] Sketch026
  ArcFitTolerance = 1e-06
  AttachmentOffset = pos=(0,0,0) rot=(1,0,0;3.14159rad)
  AttachmentSupport = -> [Pad012]
  FullyConstrained = false
  MakeInternals = false
  MapMode = 5
  sketch-geometry (6):
    g0: ArcOfCircle CenterX=-42 CenterY=37.5 CenterZ=0 NormalX=0 NormalY=0 NormalZ=1 AngleXU=0 Radius=26.6323 StartAngle=5.39176 EndAngle=10.1229
    g1: LineSegment StartX=-62.4015 StartY=20.3811 StartZ=0 EndX=-20.5819 EndY=-29.4576 EndZ=0
    g2: ArcOfCircle CenterX=-42 CenterY=37.5 CenterZ=0 NormalX=0 NormalY=0 NormalZ=1 AngleXU=0 Radius=29 StartAngle=5.39774 EndAngle=10.1229
    g3: LineSegment StartX=-20.5819 StartY=-33.1411 StartZ=0 EndX=-64.2153 EndY=18.8592 EndZ=0
    g4: LineSegment StartX=-20.5819 StartY=-29.4576 StartZ=0 EndX=-20.5819 EndY=-33.1411 EndZ=0
    g5: LineSegment StartX=-23.6446 StartY=15.0483 StartZ=0 EndX=-25.2669 EndY=16.7809 EndZ=0
  constraints (13):
    c: Angle(g1,g-1) = 0.872665
    c: Coincident(g0,g1)
    c: DistanceX(g0,g-1) = 42
    c: DistanceY(g-1,g0) = 37.5
    c: Coincident(g2,g0)
    c: Diameter(g2) = 58
    c: Angle(g3,g-1) = 0.872665
    c: Coincident(g2,g3)
    c: Vertical(g1,g3)
    c: Coincident(g4,g1)
    c: Coincident(g4,g3)
    c: Coincident(g5,g2)
    c: Coincident(g0,g5)
FEATURE [PartDesign::Pad] Pad013
  BaseFeature = -> Pad012
  Direction = (0,1e-16,1)
  Length = 5
  Length2 = 10
  Profile = -> Sketch026
  ReferenceAxis = -> Sketch026 [N_Axis]
  Refine = true
  Reversed = true
  Suppressed = false
  Type = 0
FEATURE [Sketcher::SketchObject] Sketch027
  ArcFitTolerance = 1e-06
  AttachmentSupport = -> [Pad013]
  ExternalGeometry = -> [Pad013]
  FullyConstrained = false
  MakeInternals = false
  MapMode = 5
  Placement = pos=(0,0,0) rot=(1,0,0;3.14159rad)
  sketch-geometry (4):
    g0: LineSegment StartX=-10.4578 StartY=-4 StartZ=0 EndX=-7.10141 EndY=-4e-16 EndZ=0
    g1: LineSegment StartX=-7.10141 StartY=-4e-16 StartZ=0 EndX=13 EndY=-4e-16 EndZ=0
    g2: LineSegment StartX=13 StartY=-4e-16 StartZ=0 EndX=13 EndY=-4 EndZ=0
    g3: LineSegment StartX=13 StartY=-4 StartZ=0 EndX=-10.4578 EndY=-4 EndZ=0
  constraints (9):
    c: Coincident(g0,g1)
    c: Horizontal(g1)
    c: Coincident(g1,g2)
    c: Vertical(g2)
    c: Coincident(g2,g3)
    c: Coincident(g3,g0)
    c: Angle(g3,g0) = 0.872665
    c: Horizontal(g1,g-1)
    c: Coincident(g2,g-3)
FEATURE [PartDesign::Pad] Pad014
  BaseFeature = -> Pad013
  Direction = (0,0,-1)
  Length = 14
  Length2 = 10
  Profile = -> Sketch027
  ReferenceAxis = -> Sketch027 [N_Axis]
  Refine = true
  Suppressed = false
  Type = 0
FEATURE [Sketcher::SketchObject] Sketch028
  ArcFitTolerance = 1e-06
  AttachmentSupport = -> [Pad014]
  ExternalGeometry = -> [Pad014]
  FullyConstrained = true
  MakeInternals = false
  MapMode = 5
  Placement = pos=(0,0,0) rot=(1,0,0;3.14159rad)
  sketch-geometry (4):
    g0: LineSegment StartX=-13.7082 StartY=46 StartZ=0 EndX=-17.0646 EndY=42 EndZ=0
    g1: LineSegment StartX=-17.0646 StartY=42 StartZ=0 EndX=13 EndY=42 EndZ=0
    g2: LineSegment StartX=-13.7082 StartY=46 StartZ=0 EndX=13 EndY=46 EndZ=0
    g3: LineSegment StartX=13 StartY=42 StartZ=0 EndX=13 EndY=46 EndZ=0
  constraints (10):
    c: PointOnObject(g0,g-3)
    c: Coincident(g0,g1)
    c: Coincident(g0,g-3)
    c: Coincident(g2,g0)
    c: Coincident(g3,g1)
    c: Coincident(g3,g2)
    c: Vertical(g3)
    c: Distance(g-1,g1) = 42
    c: Horizontal(g1)
    c: Coincident(g3,g-4)
FEATURE [PartDesign::Pad] Pad015
  BaseFeature = -> Pad014
  Direction = (0,0,-1)
  Length = 51
  Length2 = 10
  Profile = -> Sketch028
  ReferenceAxis = -> Sketch028 [N_Axis]
  Refine = true
  Suppressed = false
  Type = 0
FEATURE [Sketcher::SketchObject] Sketch029
  ArcFitTolerance = 1e-06
  AttachmentSupport = -> [Pad015]
  FullyConstrained = true
  MakeInternals = false
  MapMode = 5
  Placement = pos=(0,-46,0) rot=(1,0,0;1.5708rad)
  sketch-geometry (3):
    g0: ArcOfCircle CenterX=33 CenterY=-31 CenterZ=0 NormalX=0 NormalY=0 NormalZ=1 AngleXU=0 Radius=20 StartAngle=3.14159 EndAngle=4.71239
    g1: LineSegment StartX=13 StartY=-31 StartZ=0 EndX=13 EndY=-51 EndZ=0
    g2: LineSegment StartX=13 StartY=-51 StartZ=0 EndX=33 EndY=-51 EndZ=0
  constraints (9):
    c: Horizontal(g0,g0)
    c: Radius(g0) = 20
    c: Coincident(g0,g1)
    c: DistanceY(g0,g-1) = 31
    c: Distance(g0,g-2) = 33
    c: Vertical(g1)
    c: DistanceY(g1,g1) = 20
    c: Coincident(g2,g1)
    c: Tangent(g2,g0) = -1.5708
FEATURE [PartDesign::Pad] Pad016
  BaseFeature = -> Pad015
  Direction = (0,-1,2e-16)
  Length = 4
  Length2 = 10
  Profile = -> Sketch029
  ReferenceAxis = -> Sketch029 [N_Axis]
  Refine = true
  Reversed = true
  Suppressed = false
  Type = 0
FEATURE [Sketcher::SketchObject] Sketch030
  ArcFitTolerance = 1e-06
  AttachmentSupport = -> [Pad016]
  FullyConstrained = true
  MakeInternals = false
  MapMode = 5
  Placement = pos=(13,0,0) rot=(0.57735,0.57735,0.57735;2.0944rad)
  sketch-geometry (4):
    g0: LineSegment StartX=-42 StartY=0 StartZ=0 EndX=0 EndY=0 EndZ=0
    g1: LineSegment StartX=-42 StartY=3 StartZ=0 EndX=-42 EndY=0 EndZ=0
    g2: LineSegment StartX=-42 StartY=3 StartZ=0 EndX=0 EndY=3 EndZ=0
    g3: LineSegment StartX=0 StartY=0 StartZ=0 EndX=0 EndY=3 EndZ=0
  constraints (11):
    c: Coincident(g1,g0)
    c: Coincident(g1,g2)
    c: PointOnObject(g2,g-2)
    c: Horizontal(g2)
    c: Coincident(g0,g3)
    c: Coincident(g3,g2)
    c: Vertical(g1)
    c: Horizontal(g0)
    c: Coincident(g0,g-1)
    c: DistanceY(g3,g3) = 3
    c: Distance(g-2,g1) = 42
FEATURE [PartDesign::Pad] Pad017
  BaseFeature = -> Pad016
  Direction = (1,0,0)
  Length = 40
  Length2 = 10
  Profile = -> Sketch030
  ReferenceAxis = -> Sketch030 [N_Axis]
  Refine = true
  Suppressed = false
  Type = 0
FEATURE [PartDesign::Fillet] Fillet003
  Base = -> Pad017 [Edge1]
  BaseFeature = -> Pad017
  Radius = 10
  Refine = true
  SupportTransform = false
  Suppressed = false
  UseAllEdges = false
FEATURE [PartDesign::Fillet] Fillet
  Base = -> Pad017 [Edge4,Edge7,Edge12,Edge13,Edge15]
  BaseFeature = -> Pad017
  Radius = 4
  Refine = true
  SupportTransform = false
  Suppressed = false
  UseAllEdges = false
FEATURE [Sketcher::SketchObject] Sketch066
  ArcFitTolerance = 1e-06
  AttachmentSupport = -> [Fillet]
  ExternalGeometry = -> [Fillet]
  FullyConstrained = true
  MakeInternals = false
  MapMode = 5
  Placement = pos=(0,0,3) rot=(0,0,1;0rad)
  sketch-geometry (8):
    g0: LineSegment StartX=53 StartY=-3 StartZ=0 EndX=41 EndY=-3 EndZ=0
    g1: LineSegment StartX=41 StartY=-3 StartZ=0 EndX=41 EndY=-9 EndZ=0
    g2: LineSegment StartX=41 StartY=-9 StartZ=0 EndX=53 EndY=-9 EndZ=0
    g3: LineSegment StartX=53 StartY=-9 StartZ=0 EndX=53 EndY=-3 EndZ=0
    g4: LineSegment StartX=53 StartY=-39 StartZ=0 EndX=53 EndY=-33 EndZ=0
    g5: LineSegment StartX=53 StartY=-33 StartZ=0 EndX=41 EndY=-33 EndZ=0
    g6: LineSegment StartX=41 StartY=-33 StartZ=0 EndX=41 EndY=-39 EndZ=0
    g7: LineSegment StartX=41 StartY=-39 StartZ=0 EndX=53 EndY=-39 EndZ=0
  constraints (24):
    c: Coincident(g0,g1)
    c: Coincident(g1,g2)
    c: Coincident(g2,g3)
    c: Coincident(g3,g0)
    c: Horizontal(g0)
    c: Horizontal(g2)
    c: Vertical(g1)
    c: Vertical(g3)
    c: PointOnObject(g0,g-3)
    c: Coincident(g4,g5)
    c: Coincident(g5,g6)
    c: Coincident(g6,g7)
    c: Coincident(g7,g4)
    c: Vertical(g4)
    c: Vertical(g6)
    c: Horizontal(g5)
    c: Horizontal(g7)
    c: PointOnObject(g4,g-3)
    c: Distance(g-1,g0) = 3
    c: DistanceY(g1,g1) = 6
    c: Distance(g-4,g7) = 3
    c: DistanceY(g6,g6) = 6
    c: DistanceX(g2,g2) = 12
    c: DistanceX(g5,g5) = 12
FEATURE [PartDesign::Pocket] Pocket037
  BaseFeature = -> Fillet
  Direction = (0,0,-1)
  Length = 5
  Length2 = 5
  Profile = -> Sketch066
  ReferenceAxis = -> Sketch066 [N_Axis]
  Refine = true
  Suppressed = false
  Type = 0
FEATURE [PartDesign::Body] Body005  label="ThirdArmLid"
  AllowCompound = false
  Group = -> [Pad012,Sketch025,Sketch026,Pad013,Sketch027,Pad014,Sketch028,Pad015,Sketch029,Pad016,Sketch030,Pad017,Fillet003,Fillet,Sketch066,Pocket037]
  Origin = -> Origin005
  Placement = pos=(-2,0,7) rot=(0,0,1;0rad)
  Tip = -> Pocket037
COMPONENT P3 — recipe-attached ("Bodyv2", modeled in this document).
Construction recipe (the document's own serialized feature program — sketch geometry with constraints, then the solid features built on it; lengths are millimeters unless a unit is written):

FEATURE [Sketcher::SketchObject] Sketch035
  ArcFitTolerance = 1e-06
  AttachmentSupport = -> [XZ_Plane007]
  FullyConstrained = true
  MakeInternals = false
  MapMode = 5
  Placement = pos=(0,0,0) rot=(1,0,0;1.5708rad)
  expr: Constraints[15] = <<Spreadsheet001>>.UpperLowerSpace
  expr: Constraints[7] = <<Spreadsheet001>>.CenterSpace
  sketch-geometry (6):
    g0: LineSegment StartX=42.83 StartY=-37 StartZ=0 EndX=42.83 EndY=4 EndZ=0
    g1: LineSegment StartX=42.83 StartY=4 StartZ=0 EndX=-19.5 EndY=4 EndZ=0
    g2: LineSegment StartX=-19.5 StartY=-37 StartZ=0 EndX=42.83 EndY=-37 EndZ=0
    g3: Circle CenterX=31 CenterY=-24 CenterZ=0 NormalX=0 NormalY=0 NormalZ=1 AngleXU=0 Radius=7.5
    g4: LineSegment StartX=-19.5 StartY=4 StartZ=0 EndX=-19.5 EndY=-37 EndZ=0
    g5: Circle CenterX=31 CenterY=-11 CenterZ=0 NormalX=0 NormalY=0 NormalZ=1 AngleXU=0 Radius=4
  constraints (18):
    c: Coincident(g0,g1)
    c: Vertical(g0)
    c: Horizontal(g1)
    c: Horizontal(g2)
    c: Coincident(g4,g2)
    c: Vertical(g4)
    c: Coincident(g0,g2)
    c: Distance(g3,g-2) = 31
    c: Diameter(g3) = 15
    c: Diameter(g5) = 8
    c: Vertical(g3,g5)
    c: Distance(g-1,g1) = 4
    c: Distance(g-1,g2) = 37
    c: Distance(g0,g-2) = 42.83
    c: Distance(g3,g2) = 13
    c: DistanceY(g3,g5) = 13
    c: Coincident(g1,g4)
    c: Distance(g-2,g4) = 19.5
FEATURE [PartDesign::Pad] Pad019
  Direction = (0,-1,2e-16)
  Length = 42
  Length2 = 10
  Placement = pos=(0,0,0) rot=(1,0,0;1.5708rad)
  Profile = -> Sketch035
  ReferenceAxis = -> Sketch035 [N_Axis]
  Refine = true
  Suppressed = false
  Type = 0
FEATURE [Sketcher::SketchObject] Sketch036
  ArcFitTolerance = 1e-06
  AttachmentSupport = -> [Pad019]
  ExternalGeometry = -> [Pad019]
  FullyConstrained = false
  MakeInternals = false
  MapMode = 5
  Placement = pos=(0,1.8e-15,4) rot=(0,0,1;3.14159rad)
  sketch-geometry (7):
    g0: LineSegment StartX=-50.4105 StartY=38 StartZ=0 EndX=-50.4105 EndY=18.9532 EndZ=0
    g1: LineSegment StartX=41.4002 StartY=23 StartZ=0 EndX=41.4002 EndY=38 EndZ=0
    g2: LineSegment StartX=41.4002 StartY=38 StartZ=0 EndX=-50.4105 EndY=38 EndZ=0
    g3: LineSegment StartX=-50.4105 StartY=18.9532 StartZ=0 EndX=-50.4105 EndY=4 EndZ=0
    g4: LineSegment StartX=-50.4105 StartY=4 StartZ=0 EndX=-23.5 EndY=4 EndZ=0
    g5: LineSegment StartX=-23.5 StartY=4 StartZ=0 EndX=-23.5 EndY=23 EndZ=0
    g6: LineSegment StartX=-23.5 StartY=23 StartZ=0 EndX=41.4002 EndY=23 EndZ=0
  constraints (18):
    c: Coincident(g1,g2)
    c: Coincident(g2,g0)
    c: Vertical(g0)
    c: Vertical(g1)
    c: Horizontal(g2)
    c: Coincident(g3,g4)
    c: Coincident(g4,g5)
    c: Vertical(g3)
    c: Vertical(g5)
    c: Horizontal(g4)
    c: Coincident(g3,g0)
    c: Coincident(g6,g5)
    c: Coincident(g6,g1)
    c: Horizontal(g6)
    c: Distance(g-1,g4) = 4
    c: Distance(g-2,g5) = 23.5
    c: Distance(g-3,g2) = 4
    c: Distance(g-1,g6) = 23
FEATURE [PartDesign::Pocket] Pocket015
  BaseFeature = -> Pad019
  Direction = (0,0,-1)
  Length = 30
  Length2 = 5
  Placement = pos=(0,0,0) rot=(1,0,0;1.5708rad)
  Profile = -> Sketch036
  ReferenceAxis = -> Sketch036 [N_Axis]
  Refine = true
  Suppressed = false
  Type = 0
FEATURE [Sketcher::SketchObject] Sketch037
  ArcFitTolerance = 1e-06
  AttachmentSupport = -> [Pocket015]
  ExternalGeometry = -> [Pocket015]
  FullyConstrained = false
  MakeInternals = false
  MapMode = 5
  Placement = pos=(0,0,-26) rot=(0,0,1;3.14159rad)
  sketch-geometry (15):
    g0: LineSegment StartX=-40.79 StartY=30.0707 StartZ=0 EndX=-40.79 EndY=22.3263 EndZ=0
    g1: LineSegment StartX=-40.79 StartY=22.3263 StartZ=0 EndX=-8.42993 EndY=22.3263 EndZ=0
    g2: Circle CenterX=-31 CenterY=15 CenterZ=0 NormalX=0 NormalY=0 NormalZ=1 AngleXU=0 Radius=1.5
    g3: Circle CenterX=15 CenterY=25 CenterZ=0 NormalX=0 NormalY=0 NormalZ=1 AngleXU=0 Radius=1.5
    g4: Circle CenterX=0 CenterY=35 CenterZ=0 NormalX=0 NormalY=0 NormalZ=1 AngleXU=0 Radius=1.5
    g5: LineSegment StartX=-8.42993 StartY=22.3263 StartZ=0 EndX=-8.42993 EndY=15.2343 EndZ=0
    g6: LineSegment StartX=-8.42993 StartY=15.2343 StartZ=0 EndX=3.56508 EndY=15.2343 EndZ=0
    g7: LineSegment StartX=3.56508 StartY=15.2343 StartZ=0 EndX=3.56508 EndY=22.3263 EndZ=0
    g8: LineSegment StartX=3.56508 StartY=22.3263 StartZ=0 EndX=7.24123 EndY=22.3263 EndZ=0
    g9: LineSegment StartX=-16.9534 StartY=30.0707 StartZ=0 EndX=-16.9534 EndY=38 EndZ=0
    g10: LineSegment StartX=-40.79 StartY=30.0707 StartZ=0 EndX=-16.9534 EndY=30.0707 EndZ=0
    g11: LineSegment StartX=-16.9534 StartY=38 StartZ=0 EndX=9.08031 EndY=38 EndZ=0
    g12: LineSegment StartX=9.08031 StartY=38 StartZ=0 EndX=9.08031 EndY=30.0707 EndZ=0
    g13: LineSegment StartX=9.08031 StartY=30.0707 StartZ=0 EndX=7.24123 EndY=30.0707 EndZ=0
    g14: LineSegment StartX=7.24123 StartY=30.0707 StartZ=0 EndX=7.24123 EndY=22.3263 EndZ=0
  constraints (34):
    c: Coincident(g0,g1)
    c: Vertical(g0)
    c: Horizontal(g1)
    c: Diameter(g2) = 3
    c: Distance(g2,g-1) = 15
    c: Diameter(g3) = 3
    c: PointOnObject(g4,g-2)
    c: Diameter(g4) = 3
    c: DistanceY(g-1,g3) = 25
    c: DistanceY(g-1,g4) = 35
    c: Distance(g3,g-2) = 15
    c: Coincident(g5,g6)
    c: Coincident(g6,g7)
    c: Vertical(g5)
    c: Vertical(g7)
    c: Horizontal(g6)
    c: Coincident(g5,g1)
    c: Coincident(g7,g8)
    c: DistanceX(g2,g-1) = 31
    c: Vertical(g9)
    c: Coincident(g0,g10)
    c: Coincident(g10,g9)
    c: Horizontal(g10)
    c: Horizontal(g11)
    c: Coincident(g11,g12)
    c: Vertical(g12)
    c: Coincident(g12,g13)
    c: Horizontal(g13)
    c: Coincident(g13,g14)
    c: Coincident(g14,g8)
    c: Vertical(g14)
    c: Coincident(g9,g11)
    c: Horizontal(g9,g13)
    c: Horizontal(g11,g-3)
FEATURE [PartDesign::Pocket] Pocket016
  BaseFeature = -> Pocket015
  Direction = (0,0,-1)
  Length = 5
  Length2 = 5
  Placement = pos=(0,0,0) rot=(1,0,0;1.5708rad)
  Profile = -> Sketch037
  ReferenceAxis = -> Sketch037 [N_Axis]
  Refine = true
  Suppressed = false
  Type = 1
FEATURE [Sketcher::SketchObject] Sketch038
  ArcFitTolerance = 1e-06
  AttachmentSupport = -> [Pocket016]
  FullyConstrained = false
  MakeInternals = false
  MapMode = 5
  Placement = pos=(0,-42,0) rot=(1,0,0;1.5708rad)
  sketch-geometry (8):
    g0: LineSegment StartX=20 StartY=-21 StartZ=0 EndX=20 EndY=12.6879 EndZ=0
    g1: LineSegment StartX=20 StartY=12.6879 StartZ=0 EndX=-22.1888 EndY=12.6879 EndZ=0
    g2: LineSegment StartX=2.00581 StartY=-21 StartZ=0 EndX=8.1848 EndY=-30.0757 EndZ=0
    g3: LineSegment StartX=8.1848 StartY=-30.0757 StartZ=0 EndX=15.2981 EndY=-30.0757 EndZ=0
    g4: LineSegment StartX=15.2981 StartY=-30.0757 StartZ=0 EndX=20 EndY=-21 EndZ=0
    g5: LineSegment StartX=2.00581 StartY=-21 StartZ=0 EndX=2.00581 EndY=-17 EndZ=0
    g6: LineSegment StartX=2.00581 StartY=-17 StartZ=0 EndX=-22.1888 EndY=-17 EndZ=0
    g7: LineSegment StartX=-22.1888 StartY=-17 StartZ=0 EndX=-22.1888 EndY=12.6879 EndZ=0
  constraints (17):
    c: Coincident(g0,g1)
    c: Vertical(g0)
    c: Horizontal(g1)
    c: Distance(g-2,g0) = 20
    c: Coincident(g2,g3)
    c: Horizontal(g3)
    c: Coincident(g3,g4)
    c: Horizontal(g0,g2)
    c: Coincident(g0,g4)
    c: Coincident(g2,g5)
    c: Vertical(g5)
    c: Coincident(g5,g6)
    c: Coincident(g6,g7)
    c: Vertical(g7)
    c: Coincident(g1,g7)
    c: Horizontal(g6)
    c: Distance(g-3,g6) = 20
FEATURE [PartDesign::Pocket] Pocket017
  BaseFeature = -> Pocket016
  Direction = (0,1,-2e-16)
  Length = 15
  Length2 = 5
  Placement = pos=(0,0,0) rot=(1,0,0;1.5708rad)
  Profile = -> Sketch038
  ReferenceAxis = -> Sketch038 [N_Axis]
  Refine = true
  Suppressed = false
  Type = 0
FEATURE [Sketcher::SketchObject] Sketch039
  ArcFitTolerance = 1e-06
  AttachmentSupport = -> [Pocket017]
  FullyConstrained = true
  MakeInternals = false
  MapMode = 5
  Placement = pos=(0,-23,5.1e-15) rot=(1,0,0;1.5708rad)
  sketch-geometry (2):
    g0: Circle CenterX=-7.5 CenterY=-9 CenterZ=0 NormalX=0 NormalY=0 NormalZ=1 AngleXU=0 Radius=1.5
    g1: Circle CenterX=12.5 CenterY=-9 CenterZ=0 NormalX=0 NormalY=0 NormalZ=1 AngleXU=0 Radius=1.5
  constraints (6):
    c: Diameter(g0) = 3
    c: DistanceX(g0,g-1) = 7.5
    c: Diameter(g1) = 3
    c: DistanceX(g0,g1) = 20
    c: Horizontal(g0,g1)
    c: DistanceY(g0,g-1) = 9
FEATURE [PartDesign::Pocket] Pocket018
  BaseFeature = -> Pocket017
  Direction = (0,1,-2e-16)
  Length = 10
  Length2 = 5
  Placement = pos=(0,0,0) rot=(1,0,0;1.5708rad)
  Profile = -> Sketch039
  ReferenceAxis = -> Sketch039 [N_Axis]
  Refine = true
  Suppressed = false
  Type = 0
FEATURE [Sketcher::SketchObject] Sketch040
  ArcFitTolerance = 1e-06
  AttachmentSupport = -> [Pocket018]
  ExternalGeometry = -> [Pocket018]
  FullyConstrained = true
  MakeInternals = false
  MapMode = 5
  Placement = pos=(0,-1.63e-14,-37) rot=(1,0,0;3.14159rad)
  sketch-geometry (4):
    g0: LineSegment StartX=-9.08031 StartY=38 StartZ=0 EndX=-9.08031 EndY=30.0707 EndZ=0
    g1: LineSegment StartX=-9.08031 StartY=30.0707 StartZ=0 EndX=16.9534 EndY=30.0707 EndZ=0
    g2: LineSegment StartX=-9.08031 StartY=38 StartZ=0 EndX=16.9534 EndY=38 EndZ=0
    g3: LineSegment StartX=16.9534 StartY=38 StartZ=0 EndX=16.9534 EndY=30.0707 EndZ=0
  constraints (9):
    c: Vertical(g0)
    c: Coincident(g0,g1)
    c: Coincident(g0,g-5)
    c: Coincident(g1,g-4)
    c: Coincident(g0,g2)
    c: Coincident(g2,g-4)
    c: Horizontal(g2)
    c: Coincident(g2,g3)
    c: Coincident(g3,g1)
FEATURE [PartDesign::Pad] Pad020
  BaseFeature = -> Pocket018
  Direction = (0,0,-1)
  Length = 2.5
  Length2 = 10
  Placement = pos=(0,0,0) rot=(1,0,0;1.5708rad)
  Profile = -> Sketch040
  ReferenceAxis = -> Sketch040 [N_Axis]
  Refine = true
  Reversed = true
  Suppressed = false
  Type = 0
FEATURE [Sketcher::SketchObject] Sketch041
  ArcFitTolerance = 1e-06
  AttachmentSupport = -> [Pad020]
  FullyConstrained = true
  MakeInternals = false
  MapMode = 5
  Placement = pos=(0,-38,0) rot=(-1,0,0;1.5708rad)
  sketch-geometry (2):
    g0: Circle CenterX=-6 CenterY=29 CenterZ=0 NormalX=0 NormalY=0 NormalZ=1 AngleXU=0 Radius=1.5
    g1: Circle CenterX=-6 CenterY=19.5 CenterZ=0 NormalX=0 NormalY=0 NormalZ=1 AngleXU=0 Radius=1.5
  constraints (6):
    c: Diameter(g0) = 3
    c: Diameter(g1) = 3
    c: DistanceY(g-1,g1) = 19.5
    c: DistanceY(g1,g0) = 9.5
    c: Vertical(g0,g1)
    c: Distance(g1,g-2) = 6
FEATURE [PartDesign::Pocket] Pocket019
  BaseFeature = -> Pad020
  Direction = (0,-1,-2e-16)
  Length = 5
  Length2 = 5
  Placement = pos=(0,0,0) rot=(1,0,0;1.5708rad)
  Profile = -> Sketch041
  ReferenceAxis = -> Sketch041 [N_Axis]
  Refine = true
  Suppressed = false
  Type = 1
FEATURE [Sketcher::SketchObject] Sketch042
  ArcFitTolerance = 1e-06
  AttachmentSupport = -> [Pocket019]
  FullyConstrained = false
  MakeInternals = false
  MapMode = 5
  Placement = pos=(0,-3.8e-15,0) rot=(-1,0,0;1.5708rad)
  sketch-geometry (6):
    g0: ArcOfCircle CenterX=2.5 CenterY=9 CenterZ=0 NormalX=0 NormalY=0 NormalZ=1 AngleXU=0 Radius=7.75 StartAngle=2.74605 EndAngle=7.03661
    g1: LineSegment StartX=-5 StartY=23.565 StartZ=0 EndX=-5 EndY=11.9862 EndZ=0
    g2: LineSegment StartX=-5 StartY=11.9862 StartZ=0 EndX=-4.6516 EndY=11.9862 EndZ=0
    g3: LineSegment StartX=14.5 StartY=14.3021 StartZ=0 EndX=14.5 EndY=23.565 EndZ=0
    g4: LineSegment StartX=14.5 StartY=23.565 StartZ=0 EndX=-5 EndY=23.565 EndZ=0
    g5: LineSegment StartX=8.15247 StartY=14.3021 StartZ=0 EndX=14.5 EndY=14.3021 EndZ=0
  constraints (16):
    c: DistanceX(g-1,g0) = 2.5
    c: DistanceY(g-1,g0) = 9
    c: Diameter(g0) = 15.5
    c: Coincident(g1,g2)
    c: Coincident(g5,g3)
    c: Coincident(g3,g4)
    c: Coincident(g4,g1)
    c: Vertical(g1)
    c: Vertical(g3)
    c: Horizontal(g2)
    c: Horizontal(g4)
    c: Distance(g0,g1) = 7.5
    c: Distance(g0,g3) = 12
    c: Coincident(g0,g5)
    c: Coincident(g0,g2)
    c: Horizontal(g5)
FEATURE [PartDesign::Pocket] Pocket020
  BaseFeature = -> Pocket019
  Direction = (0,-1,-2e-16)
  Length = 35
  Length2 = 5
  Placement = pos=(0,0,0) rot=(1,0,0;1.5708rad)
  Profile = -> Sketch042
  ReferenceAxis = -> Sketch042 [N_Axis]
  Refine = true
  Suppressed = false
  Type = 0
FEATURE [Sketcher::SketchObject] Sketch044
  ArcFitTolerance = 1e-06
  AttachmentSupport = -> [Pocket020]
  FullyConstrained = true
  MakeInternals = false
  MapMode = 5
  Placement = pos=(0,-2.52e-14,-37) rot=(1,0,0;3.14159rad)
  sketch-geometry (1):
    g0: Circle CenterX=8 CenterY=35 CenterZ=0 NormalX=0 NormalY=0 NormalZ=1 AngleXU=0 Radius=1.5
  constraints (3):
    c: Diameter(g0) = 3
    c: Distance(g0,g-2) = 8
    c: DistanceY(g-1,g0) = 35
FEATURE [PartDesign::Pocket] Pocket022
  BaseFeature = -> Pocket020
  Direction = (0,0,1)
  Length = 5
  Length2 = 5
  Placement = pos=(0,0,0) rot=(1,0,0;1.5708rad)
  Profile = -> Sketch044
  ReferenceAxis = -> Sketch044 [N_Axis]
  Refine = true
  Suppressed = false
  Type = 0
FEATURE [PartDesign::Chamfer] Chamfer002
  Angle = 45
  Base = -> Pocket022 [Edge7,Edge1]
  BaseFeature = -> Pocket022
  ChamferType = 0
  FlipDirection = false
  Placement = pos=(0,0,0) rot=(1,0,0;1.5708rad)
  Refine = true
  Size = 4
  Size2 = 1
  SupportTransform = false
  Suppressed = false
  UseAllEdges = false
FEATURE [Sketcher::SketchObject] Sketch045
  ArcFitTolerance = 1e-06
  AttachmentSupport = -> [Chamfer002]
  FullyConstrained = false
  MakeInternals = false
  MapMode = 5
  Placement = pos=(0,-23,5.1e-15) rot=(1,0,0;1.5708rad)
  sketch-geometry (8):
    g0: ArcOfCircle CenterX=2.5 CenterY=-9 CenterZ=0 NormalX=0 NormalY=0 NormalZ=1 AngleXU=0 Radius=7.5 StartAngle=4.12969 EndAngle=5.2949
    g1: ArcOfCircle CenterX=12.5 CenterY=-9 CenterZ=0 NormalX=0 NormalY=0 NormalZ=1 AngleXU=0 Radius=2 StartAngle=5.29475 EndAngle=7.27178
    g2: LineSegment StartX=-8.59969 StartY=-7.3276 StartZ=0 EndX=-1.62383 EndY=-2.7355 EndZ=0
    g3: LineSegment StartX=-8.60796 StartY=-10.6632 StartZ=0 EndX=-1.62713 EndY=-15.2623 EndZ=0
    g4: LineSegment StartX=6.625 StartY=-2.73627 StartZ=0 EndX=13.5997 EndY=-7.32949 EndZ=0
    g5: LineSegment StartX=13.6 StartY=-10.6703 StartZ=0 EndX=6.62595 EndY=-15.2631 EndZ=0
    g6: ArcOfCircle CenterX=2.5 CenterY=-9 CenterZ=0 NormalX=0 NormalY=0 NormalZ=1 AngleXU=0 Radius=7.5 StartAngle=0.988432 EndAngle=2.15297
    g7: ArcOfCircle CenterX=-7.5 CenterY=-8.99814 CenterZ=0 NormalX=0 NormalY=0 NormalZ=1 AngleXU=0 Radius=2 StartAngle=2.15297 EndAngle=4.12525
  constraints (21):
    c: Distance(g0,g-1) = 9
    c: DistanceX(g-1,g0) = 2.5
    c: DistanceX(g0,g1) = 10
    c: Horizontal(g0,g1)
    c: Distance(g0,g2) = 7.5
    c: Distance(g0,g3) = 7.5
    c: Distance(g0,g4) = 7.5
    c: Distance(g1,g4) = 2
    c: Distance(g0,g5) = 7.5
    c: Coincident(g0,g5)
    c: Coincident(g1,g4)
    c: Coincident(g1,g5)
    c: Coincident(g6,g0)
    c: Coincident(g6,g2)
    c: Coincident(g6,g4)
    c: Radius(g7) = 2
    c: Coincident(g7,g2)
    c: Coincident(g7,g3)
    c: DistanceX(g7,g0) = 10
    c: Distance(g7,g2) = 2
    c: Coincident(g0,g3)
FEATURE [PartDesign::Pocket] Pocket023
  BaseFeature = -> Chamfer002
  Direction = (0,1,-2e-16)
  Length = 3
  Length2 = 5
  Placement = pos=(0,0,0) rot=(1,0,0;1.5708rad)
  Profile = -> Sketch045
  ReferenceAxis = -> Sketch045 [N_Axis]
  Refine = true
  Suppressed = false
  Type = 0
FEATURE [Sketcher::SketchObject] Sketch046
  ArcFitTolerance = 1e-06
  AttachmentSupport = -> [Pocket023]
  FullyConstrained = true
  MakeInternals = false
  MapMode = 5
  Placement = pos=(0,-3.8e-15,0) rot=(-1,0,0;1.5708rad)
  sketch-geometry (2):
    g0: Circle CenterX=-6.1 CenterY=29 CenterZ=0 NormalX=0 NormalY=0 NormalZ=1 AngleXU=0 Radius=3
    g1: Circle CenterX=-6.1 CenterY=19.5 CenterZ=0 NormalX=0 NormalY=0 NormalZ=1 AngleXU=0 Radius=3
  constraints (6):
    c: Diameter(g0) = 6
    c: Diameter(g1) = 6
    c: DistanceY(g-1,g1) = 19.5
    c: DistanceY(g1,g0) = 9.5
    c: Vertical(g0,g1)
    c: DistanceX(g0,g-1) = 6.1
FEATURE [PartDesign::Pocket] Pocket024
  BaseFeature = -> Pocket023
  Direction = (0,-1,-2e-16)
  Length = 25
  Length2 = 5
  Placement = pos=(0,0,0) rot=(1,0,0;1.5708rad)
  Profile = -> Sketch046
  ReferenceAxis = -> Sketch046 [N_Axis]
  Refine = true
  Suppressed = false
  Type = 0
FEATURE [Sketcher::SketchObject] Sketch047
  ArcFitTolerance = 1e-06
  AttachmentSupport = -> [Pocket024]
  FullyConstrained = true
  MakeInternals = false
  MapMode = 5
  Placement = pos=(0,1.8e-15,4) rot=(0,0,1;3.14159rad)
  sketch-geometry (1):
    g0: Circle CenterX=15 CenterY=25 CenterZ=0 NormalX=0 NormalY=0 NormalZ=1 AngleXU=0 Radius=3
  constraints (3):
    c: Diameter(g0) = 6
    c: DistanceX(g-1,g0) = 15
    c: DistanceY(g-1,g0) = 25
FEATURE [PartDesign::Pocket] Pocket025
  BaseFeature = -> Pocket024
  Direction = (0,0,-1)
  Length = 35
  Length2 = 5
  Placement = pos=(0,0,0) rot=(1,0,0;1.5708rad)
  Profile = -> Sketch047
  ReferenceAxis = -> Sketch047 [N_Axis]
  Refine = true
  Suppressed = false
  Type = 0
FEATURE [Sketcher::SketchObject] Sketch055
  ArcFitTolerance = 1e-06
  AttachmentSupport = -> [Pocket025]
  FullyConstrained = true
  MakeInternals = false
  MapMode = 5
  Placement = pos=(0,-3.8e-15,0) rot=(-1,0,0;1.5708rad)
  sketch-geometry (1):
    g0: Circle CenterX=2.5 CenterY=9 CenterZ=0 NormalX=0 NormalY=0 NormalZ=1 AngleXU=0 Radius=12.5
  constraints (3):
    c: DistanceX(g-1,g0) = 2.5
    c: DistanceY(g-1,g0) = 9
    c: Diameter(g0) = 25
FEATURE [PartDesign::Pocket] Pocket031
  BaseFeature = -> Pocket025
  Direction = (0,-1,-2e-16)
  Length = 15
  Length2 = 5
  Placement = pos=(0,0,0) rot=(1,0,0;1.5708rad)
  Profile = -> Sketch055
  ReferenceAxis = -> Sketch055 [N_Axis]
  Refine = true
  Suppressed = false
  Type = 0
FEATURE [Sketcher::SketchObject] Sketch056
  ArcFitTolerance = 1e-06
  AttachmentSupport = -> [Pocket031]
  ExternalGeometry = -> [Pocket031]
  FullyConstrained = false
  MakeInternals = false
  MapMode = 5
  Placement = pos=(0,1.8e-15,4) rot=(0,0,1;3.14159rad)
  sketch-geometry (4):
    g0: LineSegment StartX=-47.4799 StartY=15 StartZ=0 EndX=-47.4799 EndY=-6.21618 EndZ=0
    g1: LineSegment StartX=-47.4799 StartY=-6.21618 StartZ=0 EndX=23.4788 EndY=-6.21618 EndZ=0
    g2: LineSegment StartX=23.4788 StartY=-6.21618 StartZ=0 EndX=23.4788 EndY=15 EndZ=0
    g3: LineSegment StartX=23.4788 StartY=15 StartZ=0 EndX=-47.4799 EndY=15 EndZ=0
  constraints (9):
    c: Coincident(g0,g1)
    c: Coincident(g1,g2)
    c: Coincident(g2,g3)
    c: Coincident(g3,g0)
    c: Vertical(g0)
    c: Vertical(g2)
    c: Horizontal(g1)
    c: Horizontal(g3)
    c: Distance(g-1,g3) = 15
FEATURE [PartDesign::Pocket] Pocket032
  BaseFeature = -> Pocket031
  Direction = (0,0,-1)
  Length = 5
  Length2 = 5
  Placement = pos=(0,0,0) rot=(1,0,0;1.5708rad)
  Profile = -> Sketch056
  ReferenceAxis = -> Sketch056 [N_Axis]
  Refine = true
  Suppressed = false
  Type = 0
FEATURE [PartDesign::Chamfer] Chamfer003
  Angle = 40
  Base = -> Pocket032 [Edge48,Edge44]
  BaseFeature = -> Pocket032
  ChamferType = 2
  FlipDirection = false
  Placement = pos=(0,0,0) rot=(1,0,0;1.5708rad)
  Refine = true
  Size = 7
  Size2 = 1
  SupportTransform = false
  Suppressed = false
  UseAllEdges = false
FEATURE [Sketcher::SketchObject] Sketch059
  ArcFitTolerance = 1e-06
  AttachmentSupport = -> [Chamfer003]
  FullyConstrained = false
  MakeInternals = false
  MapMode = 5
  Placement = pos=(0,1.8e-15,4) rot=(0,0,1;3.14159rad)
  sketch-geometry (4):
    g0: LineSegment StartX=-49.2069 StartY=46.6697 StartZ=0 EndX=-49.2069 EndY=31.247 EndZ=0
    g1: LineSegment StartX=-49.2069 StartY=31.247 StartZ=0 EndX=-12.1923 EndY=31.247 EndZ=0
    g2: LineSegment StartX=-12.1923 StartY=31.247 StartZ=0 EndX=-12.1923 EndY=46.6697 EndZ=0
    g3: LineSegment StartX=-12.1923 StartY=46.6697 StartZ=0 EndX=-49.2069 EndY=46.6697 EndZ=0
  constraints (8):
    c: Coincident(g0,g1)
    c: Coincident(g1,g2)
    c: Coincident(g2,g3)
    c: Coincident(g3,g0)
    c: Vertical(g0)
    c: Vertical(g2)
    c: Horizontal(g1)
    c: Horizontal(g3)
FEATURE [PartDesign::Pocket] Pocket
  BaseFeature = -> Chamfer003
  Direction = (0,0,-1)
  Length = 2
  Length2 = 5
  Placement = pos=(0,0,0) rot=(1,0,0;1.5708rad)
  Profile = -> Sketch059
  ReferenceAxis = -> Sketch059 [N_Axis]
  Refine = true
  Suppressed = false
  Type = 0
FEATURE [Sketcher::SketchObject] Sketch
  ArcFitTolerance = 1e-06
  AttachmentSupport = -> [Pocket]
  ExternalGeometry = -> [Pocket]
  FullyConstrained = true
  MakeInternals = false
  MapMode = 5
  Placement = pos=(0,0,2) rot=(0,0,1;3.14159rad)
  sketch-geometry (4):
    g0: LineSegment StartX=-20 StartY=42 StartZ=0 EndX=-29 EndY=42 EndZ=0
    g1: LineSegment StartX=-29 StartY=42 StartZ=0 EndX=-29 EndY=33 EndZ=0
    g2: LineSegment StartX=-29 StartY=33 StartZ=0 EndX=-20 EndY=33 EndZ=0
    g3: LineSegment StartX=-20 StartY=33 StartZ=0 EndX=-20 EndY=42 EndZ=0
  constraints (11):
    c: Coincident(g0,g1)
    c: Coincident(g1,g2)
    c: Coincident(g2,g3)
    c: Coincident(g3,g0)
    c: Horizontal(g0)
    c: Horizontal(g2)
    c: Vertical(g1)
    c: Vertical(g3)
    c: Distance(g1,g3) = 9
    c: Distance(g0,g2) = 9
    c: Coincident(g0,g-3)
FEATURE [PartDesign::Pad] Pad
  BaseFeature = -> Pocket
  Direction = (0,0,1)
  Length = 4
  Length2 = 10
  Placement = pos=(0,0,0) rot=(1,0,0;1.5708rad)
  Profile = -> Sketch
  ReferenceAxis = -> Sketch [N_Axis]
  Refine = true
  Reversed = true
  Suppressed = false
  Type = 0
FEATURE [Sketcher::SketchObject] Sketch060
  ArcFitTolerance = 1e-06
  AttachmentSupport = -> [Pad]
  ExternalGeometry = -> [Pad]
  FullyConstrained = true
  MakeInternals = false
  MapMode = 5
  Placement = pos=(0,7e-16,2) rot=(0,0,1;3.14159rad)
  sketch-geometry (1):
    g0: Circle CenterX=-24.5 CenterY=37.5 CenterZ=0 NormalX=0 NormalY=0 NormalZ=1 AngleXU=0 Radius=2
  constraints (2):
    c: Diameter(g0) = 4
    c: Symmetric(g-4,g-3,g0)
FEATURE [PartDesign::Pocket] Pocket034
  BaseFeature = -> Pad
  Direction = (0,0,-1)
  Length = 5
  Length2 = 5
  Placement = pos=(0,0,0) rot=(1,0,0;1.5708rad)
  Profile = -> Sketch060
  ReferenceAxis = -> Sketch060 [N_Axis]
  Refine = true
  Suppressed = false
  Type = 0
FEATURE [Sketcher::SketchObject] Sketch064
  ArcFitTolerance = 1e-06
  AttachmentSupport = -> [Pocket034]
  FullyConstrained = true
  MakeInternals = false
  MapMode = 5
  Placement = pos=(0,0,-1) rot=(0,0,1;3.14159rad)
  sketch-geometry (1):
    g0: Circle CenterX=-19.4 CenterY=4 CenterZ=0 NormalX=0 NormalY=0 NormalZ=1 AngleXU=0 Radius=2
  constraints (3):
    c: Diameter(g0) = 4
    c: Distance(g0,g-1) = 4
    c: DistanceX(g0,g-1) = 19.4
FEATURE [PartDesign::Pocket] Pocket036
  BaseFeature = -> Pocket034
  Direction = (0,0,-1)
  Length = 5
  Length2 = 5
  Placement = pos=(0,0,0) rot=(1,0,0;1.5708rad)
  Profile = -> Sketch064
  ReferenceAxis = -> Sketch064 [N_Axis]
  Refine = true
  Suppressed = false
  Type = 0
FEATURE [PartDesign::Body] Body007  label="Bodyv2"
  AllowCompound = false
  Group = -> [Sketch035,Pad019,Sketch036,Pocket015,Sketch037,Pocket016,Sketch038,Pocket017,Sketch039,Pocket018,Sketch040,Pad020,Sketch041,Pocket019,Sketch042,Pocket020,Sketch044,Pocket022,Chamfer002,Sketch045,Pocket023,Sketch046,Pocket024,Sketch047,Pocket025,Sketch055,Pocket031,Sketch056,Pocket032,Chamfer003,Sketch059,Pocket,Sketch,Pad,Sketch060,Pocket034,Sketch064,Pocket036]
  Origin = -> Origin007
  Placement = pos=(0,0,0) rot=(0,0,0;0rad)
  Tip = -> Pocket036
COMPONENT P4 — recipe-attached ("SmallGear001", modeled in this document).
Construction recipe (the document's own serialized feature program — sketch geometry with constraints, then the solid features built on it; lengths are millimeters unless a unit is written):

FEATURE [PartDesign::FeaturePython] InvoluteGear001  label="InvoluteGear002"  # WARN: FeaturePython — macro-defined, semantics opaque (R4)
  AttacherType = Attacher::AttachEngine3D
  Suppressed = false
  addendum_diameter = 16
  angular_backlash = 0
  axle_hole = false
  axle_holesize = 10
  backlash = 0
  clearance = 0.25
  double_helix = false
  head = 0
  head_fillet = 0
  height = 5
  helix_angle = 0
  module = 1
  num_teeth = 14
  numpoints = 20
  offset_hole = false
  offset_holeoffset = 10
  offset_holesize = 10
  pitch_diameter = 14
  pressure_angle = 20
  properties_from_tool = false
  reversed_backlash = false
  root_diameter = 11.5
  root_fillet = 0
  shift = 0
  simple = false
  transverse_pitch = 3.14159
  traverse_module = 1
  undercut = false
  version = 1.3.0
  expr: angular_backlash = backlash / pitch_diameter * 360 ° / pi
FEATURE [Sketcher::SketchObject] Sketch043
  ArcFitTolerance = 1e-06
  AttachmentSupport = -> [InvoluteGear001]
  FullyConstrained = false
  MakeInternals = false
  MapMode = 5
  Placement = pos=(0,0,5) rot=(0,0,1;0rad)
  sketch-geometry (2):
    g0: ArcOfCircle CenterX=0 CenterY=0 CenterZ=0 NormalX=0 NormalY=0 NormalZ=1 AngleXU=0 Radius=1.5 StartAngle=2.36272 EndAngle=7.06206
    g1: LineSegment StartX=-1.06756 StartY=1.05372 StartZ=0 EndX=1.06756 EndY=1.05372 EndZ=0
  constraints (5):
    c: Diameter(g0) = 3
    c: Coincident(g0,g-1)
    c: Horizontal(g1)
    c: Coincident(g0,g1)
    c: Coincident(g1,g0)
FEATURE [PartDesign::Pocket] Pocket021
  BaseFeature = -> InvoluteGear001
  Direction = (0,0,-1)
  Length = 5
  Length2 = 5
  Profile = -> Sketch043
  ReferenceAxis = -> Sketch043 [N_Axis]
  Refine = true
  Suppressed = false
  Type = 1
FEATURE [PartDesign::Body] Body008  label="SmallGear001"
  AllowCompound = false
  Group = -> [InvoluteGear001,Sketch043,Pocket021]
  Origin = -> Origin008
  Placement = pos=(2.5,-24,-9) rot=(1,0,0;1.5708rad)
  Tip = -> Pocket021
COMPONENT P5 — recipe-attached ("SmallGear003", modeled in this document).
Construction recipe (the document's own serialized feature program — sketch geometry with constraints, then the solid features built on it; lengths are millimeters unless a unit is written):

FEATURE [PartDesign::FeaturePython] InvoluteGear002  label="InvoluteGear003"  # WARN: FeaturePython — macro-defined, semantics opaque (R4)
  AttacherType = Attacher::AttachEngine3D
  Suppressed = false
  addendum_diameter = 17
  angular_backlash = 0
  axle_hole = false
  axle_holesize = 10
  backlash = 0
  clearance = 0.25
  double_helix = false
  head = 0
  head_fillet = 0
  height = 5
  helix_angle = 0
  module = 1
  num_teeth = 14
  numpoints = 20
  offset_hole = false
  offset_holeoffset = 10
  offset_holesize = 10
  pitch_diameter = 14
  pressure_angle = 20
  properties_from_tool = false
  reversed_backlash = false
  root_diameter = 11.5
  root_fillet = 0
  shift = 0
  simple = false
  transverse_pitch = 3.14159
  traverse_module = 1
  undercut = false
  version = 1.3.0
  expr: angular_backlash = backlash / pitch_diameter * 360 ° / pi
FEATURE [Sketcher::SketchObject] Sketch048
  ArcFitTolerance = 1e-06
  AttachmentSupport = -> [InvoluteGear002]
  FullyConstrained = false
  MakeInternals = false
  MapMode = 5
  Placement = pos=(0,0,5) rot=(0,0,1;0rad)
  sketch-geometry (60):
    g0: LineSegment StartX=4.35022 StartY=-0.224286 StartZ=0 EndX=4.35022 EndY=0.224286 EndZ=0
    g1: BSplineCurve PolesCount=22 KnotsCount=20 Degree=3 IsPeriodic=0
    g2: LineSegment StartX=3.28915 StartY=0.63065 StartZ=0 EndX=2.52795 EndY=0.4847 EndZ=0
    g3: LineSegment StartX=2.52795 StartY=0.4847 StartZ=0 EndX=2.24808 EndY=1.25363 EndZ=0
    g4: LineSegment StartX=2.24808 StartY=1.25363 StartZ=0 EndX=2.92501 EndY=1.63112 EndZ=0
    g5: BSplineCurve PolesCount=22 KnotsCount=20 Degree=3 IsPeriodic=0
    g6: BSplineCurve PolesCount=2 KnotsCount=2 Degree=1 IsPeriodic=0
    g7: BSplineCurve PolesCount=22 KnotsCount=20 Degree=3 IsPeriodic=0
    g8: BSplineCurve PolesCount=2 KnotsCount=2 Degree=1 IsPeriodic=0
    g9: BSplineCurve PolesCount=2 KnotsCount=2 Degree=1 IsPeriodic=0
    g10: BSplineCurve PolesCount=2 KnotsCount=2 Degree=1 IsPeriodic=0
    g11: BSplineCurve PolesCount=22 KnotsCount=20 Degree=3 IsPeriodic=0
    g12: BSplineCurve PolesCount=2 KnotsCount=2 Degree=1 IsPeriodic=0
    g13: BSplineCurve PolesCount=22 KnotsCount=20 Degree=3 IsPeriodic=0
    g14: BSplineCurve PolesCount=2 KnotsCount=2 Degree=1 IsPeriodic=0
    g15: BSplineCurve PolesCount=2 KnotsCount=2 Degree=1 IsPeriodic=0
    g16: BSplineCurve PolesCount=2 KnotsCount=2 Degree=1 IsPeriodic=0
    g17: BSplineCurve PolesCount=22 KnotsCount=20 Degree=3 IsPeriodic=0
    g18: BSplineCurve PolesCount=2 KnotsCount=2 Degree=1 IsPeriodic=0
    g19: BSplineCurve PolesCount=22 KnotsCount=20 Degree=3 IsPeriodic=0
    g20: BSplineCurve PolesCount=2 KnotsCount=2 Degree=1 IsPeriodic=0
    g21: BSplineCurve PolesCount=2 KnotsCount=2 Degree=1 IsPeriodic=0
    g22: BSplineCurve PolesCount=2 KnotsCount=2 Degree=1 IsPeriodic=0
    g23: BSplineCurve PolesCount=22 KnotsCount=20 Degree=3 IsPeriodic=0
    g24: BSplineCurve PolesCount=2 KnotsCount=2 Degree=1 IsPeriodic=0
    g25: BSplineCurve PolesCount=22 KnotsCount=20 Degree=3 IsPeriodic=0
    g26: BSplineCurve PolesCount=2 KnotsCount=2 Degree=1 IsPeriodic=0
    g27: BSplineCurve PolesCount=2 KnotsCount=2 Degree=1 IsPeriodic=0
    g28: BSplineCurve PolesCount=2 KnotsCount=2 Degree=1 IsPeriodic=0
    g29: BSplineCurve PolesCount=22 KnotsCount=20 Degree=3 IsPeriodic=0
    g30: BSplineCurve PolesCount=2 KnotsCount=2 Degree=1 IsPeriodic=0
    g31: BSplineCurve PolesCount=22 KnotsCount=20 Degree=3 IsPeriodic=0
    g32: BSplineCurve PolesCount=2 KnotsCount=2 Degree=1 IsPeriodic=0
    g33: BSplineCurve PolesCount=2 KnotsCount=2 Degree=1 IsPeriodic=0
    g34: BSplineCurve PolesCount=2 KnotsCount=2 Degree=1 IsPeriodic=0
    g35: BSplineCurve PolesCount=22 KnotsCount=20 Degree=3 IsPeriodic=0
    g36: BSplineCurve PolesCount=2 KnotsCount=2 Degree=1 IsPeriodic=0
    g37: BSplineCurve PolesCount=2 KnotsCount=2 Degree=1 IsPeriodic=0
    g38: BSplineCurve PolesCount=2 KnotsCount=2 Degree=1 IsPeriodic=0
    g39: BSplineCurve PolesCount=22 KnotsCount=20 Degree=3 IsPeriodic=0
    g40: BSplineCurve PolesCount=2 KnotsCount=2 Degree=1 IsPeriodic=0
    g41: BSplineCurve PolesCount=22 KnotsCount=20 Degree=3 IsPeriodic=0
    g42: BSplineCurve PolesCount=2 KnotsCount=2 Degree=1 IsPeriodic=0
    g43: BSplineCurve PolesCount=2 KnotsCount=2 Degree=1 IsPeriodic=0
    g44: BSplineCurve PolesCount=2 KnotsCount=2 Degree=1 IsPeriodic=0
    g45: BSplineCurve PolesCount=22 KnotsCount=20 Degree=3 IsPeriodic=0
    g46: BSplineCurve PolesCount=2 KnotsCount=2 Degree=1 IsPeriodic=0
    g47: BSplineCurve PolesCount=22 KnotsCount=20 Degree=3 IsPeriodic=0
    g48: BSplineCurve PolesCount=2 KnotsCount=2 Degree=1 IsPeriodic=0
    g49: BSplineCurve PolesCount=2 KnotsCount=2 Degree=1 IsPeriodic=0
    g50: BSplineCurve PolesCount=2 KnotsCount=2 Degree=1 IsPeriodic=0
    g51: BSplineCurve PolesCount=22 KnotsCount=20 Degree=3 IsPeriodic=0
    g52-g55: Circle [constr] x4 (B-spline internal-alignment scaffolding for g56; pole/knot coordinates omitted)
    g56: BSplineCurve PolesCount=4 KnotsCount=2 Degree=3 IsPeriodic=0
    g57: GeomPoint [constr] X=-2.19073 Y=-2.53316 Z=0
    g58: GeomPoint [constr] X=-2.36935 Y=-3.65525 Z=0
    g59: LineSegment StartX=-2.36935 StartY=-3.65525 StartZ=0 EndX=-1.98087 EndY=-3.87955 EndZ=0
  constraints (63):
    c: Coincident(g12,g13)
    c: Coincident(g11,g12)
    c: Coincident(g10,g11)
    c: Coincident(g9,g10)
    c: Coincident(g8,g9)
    c: Coincident(g7,g8)
    c: Coincident(g6,g7)
    c: Coincident(g4,g5)
    c: Coincident(g3,g4)
    c: Coincident(g2,g3)
    c: Coincident(g1,g2)
    c: Coincident(g0,g1)
    c: Coincident(g51,g0)
    c: Coincident(g5,g6)
    c: Coincident(g50,g51)
    c: Coincident(g49,g50)
    c: Coincident(g48,g49)
    c: Coincident(g47,g48)
    c: Coincident(g46,g47)
    c: Coincident(g45,g46)
    c: Coincident(g44,g45)
    c: Coincident(g43,g44)
    c: Coincident(g42,g43)
    c: Coincident(g41,g42)
    c: Coincident(g40,g41)
    c: Coincident(g38,g39)
    c: Coincident(g37,g38)
    c: Coincident(g36,g37)
    c: Coincident(g35,g36)
    c: Coincident(g39,g40)
    c: Coincident(g33,g34)
    c: Equal(g52,g53)
    c: Equal(g52,g54)
    c: Equal(g52,g55)
    c: InternalAlignment(g52-g55 -> g56) x4
    c: InternalAlignment(g57,g56)
    c: InternalAlignment(g58,g56)
    c: Coincident(g52,g34)
    c: Coincident(g55,g54)
    c: Coincident(g59,g56)
    c: Coincident(g59,g35)
    c: Coincident(g32,g33)
    c: Coincident(g31,g32)
    c: Coincident(g27,g28)
    c: Coincident(g28,g29)
    c: Coincident(g29,g30)
    c: Coincident(g30,g31)
    c: Coincident(g26,g27)
    c: Coincident(g25,g26)
    c: Coincident(g24,g25)
    c: Coincident(g23,g24)
    c: Coincident(g22,g23)
    c: Coincident(g21,g22)
    c: Coincident(g20,g21)
    c: Coincident(g19,g20)
    c: Coincident(g18,g19)
    c: Coincident(g17,g18)
    c: Coincident(g16,g17)
    c: Coincident(g15,g16)
    c: Coincident(g14,g15)
    c: Coincident(g13,g14)
    c: Coincident(g34,g56)
    c: Coincident(g34,g57)
FEATURE [PartDesign::Pocket] Pocket026
  BaseFeature = -> InvoluteGear002
  Direction = (0,0,-1)
  Length = 5
  Length2 = 5
  Profile = -> Sketch048
  ReferenceAxis = -> Sketch048 [N_Axis]
  Refine = true
  Reversed = true
  Suppressed = false
  Type = 0
FEATURE [PartDesign::Body] Body009  label="SmallGear003"
  AllowCompound = false
  Group = -> [InvoluteGear002,Sketch048,Pocket026]
  Origin = -> Origin009
  Placement = pos=(2.5,-24,-9) rot=(1,0,0;1.5708rad)
  Tip = -> Pocket026
COMPONENT P6 — geometry summary ("PCB_Arm2"; no construction recipe available for this part):
  bounding box: 50.0 x 50.0 x 5.2 mm
  tessellated surface: 20,328 triangles
  volume: 3142 mm^3 (24% of its bounding box)
COMPONENT P7 — recipe-attached ("QuaterGear", a linked part whose construction recipe lives in a companion FreeCAD document of the same project; that document's serialized recipe follows).
Construction recipe (the companion document, serialized — sketch geometry with constraints, then the solid features built on it; lengths are millimeters unless a unit is written):

FCSTD DOCUMENT  (FreeCAD 1.0R39319 (Git))
Label: QuaterGear
License: All rights reserved
LicenseURL: https://en.wikipedia.org/wiki/All_rights_reserved
objects: Sketcher::SketchObject×3, PartDesign::Pocket×2, PartDesign::FeaturePython×1, App::Link×1, PartDesign::Pad×1, PartDesign::Body×1
note: 18 computed .brp shape members not serialized (recipe doc carries the construction recipe); baked Part::Feature solids carry a one-line shape summary decoded from their .brp
EXTERNAL_REF file=Robot.FCStd obj=Spreadsheet

FEATURE [PartDesign::FeaturePython] InvoluteGear001  # WARN: FeaturePython — macro-defined, semantics opaque (R4)
  AttacherType = Attacher::AttachEngine3D
  Placement = pos=(0,0,0) rot=(-1,0,0;4.71239rad)
  Suppressed = false
  addendum_diameter = 50
  angular_backlash = 0
  axle_hole = false
  axle_holesize = 10
  backlash = 0
  clearance = 2.25
  double_helix = false
  head = 0
  head_fillet = 0
  height = 10
  helix_angle = 0
  module = 1
  num_teeth = 50
  numpoints = 20
  offset_hole = false
  offset_holeoffset = 10
  offset_holesize = 10
  pitch_diameter = 50
  pressure_angle = 20
  properties_from_tool = false
  reversed_backlash = false
  root_diameter = 43.5
  root_fillet = 0
  shift = 0
  simple = false
  transverse_pitch = 3.14159
  traverse_module = 1
  undercut = false
  version = 1.3.0
  expr: angular_backlash = backlash / pitch_diameter * 360 ° / pi
FEATURE [Sketcher::SketchObject] Sketch
  ArcFitTolerance = 1e-06
  AttachmentSupport = -> [InvoluteGear001]
  FullyConstrained = false
  MakeInternals = false
  MapMode = 5
  Placement = pos=(0,-10,0) rot=(1,0,0;1.5708rad)
  expr: Constraints[10] = 360 - <<Spreadsheet>>.CutAngle * 2
  expr: Constraints[12] = <<Spreadsheet>>.ShaftDiameter * 2
  expr: Constraints[2] = <<Spreadsheet>>.CutAngle
  expr: Constraints[3] = 180 - <<Spreadsheet>>.CutAngle
  expr: Constraints[9] = 0 mm
  sketch-geometry (8):
    g0: ArcOfCircle CenterX=0 CenterY=0 CenterZ=0 NormalX=0 NormalY=0 NormalZ=1 AngleXU=0 Radius=9 StartAngle=2.35358 EndAngle=7.06597
    g1: LineSegment StartX=6.38059 StartY=6.34728 StartZ=0 EndX=39.2109 EndY=39.1775 EndZ=0
    g2: LineSegment StartX=-6.34728 StartY=6.38059 StartZ=0 EndX=-39.1775 EndY=39.2109 EndZ=0
    g3: ArcOfCircle CenterX=0 CenterY=0 CenterZ=0 NormalX=0 NormalY=0 NormalZ=1 AngleXU=0 Radius=55.429 StartAngle=2.35577 EndAngle=7.06816
    g4: ArcOfCircle CenterX=0 CenterY=0 CenterZ=0 NormalX=0 NormalY=0 NormalZ=1 AngleXU=0 Radius=6 StartAngle=1.82348 EndAngle=7.60029
    g5: LineSegment StartX=-1.5 StartY=8 StartZ=0 EndX=-1.5 EndY=5.80948 EndZ=0
    g6: LineSegment StartX=1.50588 StartY=5.80795 StartZ=0 EndX=1.50588 EndY=8 EndZ=0
    g7: LineSegment StartX=1.50588 StartY=8 StartZ=0 EndX=-1.5 EndY=8 EndZ=0
  constraints (22):
    c: Diameter(g0) = 18
    c: PointOnObject(g0,g-2)
    c: Angle(g-1,g1) = 0.785398
    c: Angle(g-1,g2) = 2.35619
    c: Coincident(g3,g0)
    c: Coincident(g2,g3)
    c: Coincident(g1,g3)
    c: Coincident(g2,g0)
    c: Coincident(g1,g0)
    c: DistanceY(g0,g-1) = 0
    c: Angle(g0) = 4.71239
    c: Coincident(g4,g0)
    c: Diameter(g4) = 12
    c: Coincident(g6,g7)
    c: Coincident(g7,g5)
    c: Vertical(g5)
    c: Vertical(g6)
    c: Horizontal(g7)
    c: Distance(g-2,g5) = 1.5
    c: Distance(g4,g7) = 2
    c: Coincident(g5,g4)
    c: Coincident(g6,g4)
FEATURE [PartDesign::Pocket] Pocket
  BaseFeature = -> InvoluteGear001
  Direction = (0,1,-2e-16)
  Length = 5
  Length2 = 5
  Placement = pos=(0,0,0) rot=(-1,0,0;4.71239rad)
  Profile = -> Sketch
  ReferenceAxis = -> Sketch [N_Axis]
  Refine = true
  Suppressed = false
  Type = 1
FEATURE [App::Link] Link  label="Spreadsheet"
  LinkedObject = -> <external Robot.FCStd>#Spreadsheet
FEATURE [Sketcher::SketchObject] Sketch001
  ArcFitTolerance = 1e-06
  AttachmentSupport = -> [Pocket]
  FullyConstrained = true
  MakeInternals = false
  MapMode = 5
  Placement = pos=(0,-10,0) rot=(1,0,0;1.5708rad)
  sketch-geometry (1):
    g0: Circle CenterX=0 CenterY=0 CenterZ=0 NormalX=0 NormalY=0 NormalZ=1 AngleXU=0 Radius=30
  constraints (2):
    c: Diameter(g0) = 60
    c: Coincident(g0,g-1)
FEATURE [PartDesign::Pocket] Pocket001
  BaseFeature = -> Pocket
  Direction = (0,1,-2e-16)
  Length = 5
  Length2 = 5
  Placement = pos=(0,0,0) rot=(-1,0,0;4.71239rad)
  Profile = -> Sketch001
  ReferenceAxis = -> Sketch001 [N_Axis]
  Refine = true
  Suppressed = false
  Type = 0
FEATURE [Sketcher::SketchObject] Sketch002
  ArcFitTolerance = 1e-06
  AttachmentSupport = -> [Pocket001]
  FullyConstrained = false
  MakeInternals = false
  MapMode = 5
  Placement = pos=(0,-5,0) rot=(1,0,0;1.5708rad)
  sketch-geometry (4):
    g0: ArcOfCircle CenterX=0 CenterY=0 CenterZ=0 NormalX=0 NormalY=0 NormalZ=1 AngleXU=0 Radius=25 StartAngle=1.41976 EndAngle=1.73335
    g1: ArcOfCircle CenterX=-3.56037 CenterY=21.71 CenterZ=0 NormalX=0 NormalY=0 NormalZ=1 AngleXU=0 Radius=3 StartAngle=1.73335 EndAngle=4.87494
    g2: ArcOfCircle CenterX=3.31009 CenterY=21.7496 CenterZ=0 NormalX=0 NormalY=0 NormalZ=1 AngleXU=0 Radius=3 StartAngle=4.56136 EndAngle=7.70295
    g3: ArcOfCircle CenterX=0 CenterY=0 CenterZ=0 NormalX=0 NormalY=0 NormalZ=1 AngleXU=0 Radius=19 StartAngle=1.41976 EndAngle=1.73335
  constraints (8):
    c: Coincident(g0,g3)
    c: Tangent(g3,g2) = 1.5708
    c: Tangent(g3,g1) = 1.5708
    c: Tangent(g0,g2) = -1.5708
    c: Tangent(g0,g1) = -1.5708
    c: Coincident(g0,g-1)
    c: Radius(g2) = 3
    c: Distance(g2,g-1) = 22
FEATURE [PartDesign::Pad] Pad
  BaseFeature = -> Pocket001
  Direction = (0,-1,2e-16)
  Length = 6.5
  Length2 = 10
  Placement = pos=(0,0,0) rot=(-1,0,0;4.71239rad)
  Profile = -> Sketch002
  ReferenceAxis = -> Sketch002 [N_Axis]
  Refine = true
  Suppressed = false
  Type = 0
FEATURE [PartDesign::Body] Body  label="QuaterGear"
  AllowCompound = false
  Group = -> [InvoluteGear001,Sketch,Pocket,Sketch001,Pocket001,Sketch002,Pad]
  Origin = -> Origin001
  Tip = -> Pad
COMPONENT P8 — geometry summary ("Limit switch"; no construction recipe available for this part):
  bounding box: 20.0 x 15.2 x 6.6 mm
  tessellated surface: 3,560 triangles
  volume: 1270 mm^3 (63% of its bounding box)
  symmetry: mirror-symmetric across its y mid-plane
COMPONENT P9 — geometry summary ("GM12-15BY"; no construction recipe available for this part):
  bounding box: 32.0 x 24.0 x 15.0 mm
  tessellated surface: 11,560 triangles
  volume: 3996 mm^3 (35% of its bounding box)
COMPONENT P10 — recipe-attached ("MainShaft", modeled in this document).
Construction recipe (the document's own serialized feature program — sketch geometry with constraints, then the solid features built on it; lengths are millimeters unless a unit is written):

FEATURE [Sketcher::SketchObject] Sketch004
  ArcFitTolerance = 1e-06
  AttachmentSupport = -> [XZ_Plane003]
  FullyConstrained = false
  MakeInternals = false
  MapMode = 5
  Placement = pos=(0,0,0) rot=(1,0,0;1.5708rad)
  sketch-geometry (4):
    g0: ArcOfCircle CenterX=0 CenterY=0 CenterZ=0 NormalX=0 NormalY=0 NormalZ=1 AngleXU=0 Radius=6 StartAngle=0.243488 EndAngle=6.0397
    g1: LineSegment StartX=8 StartY=1.44654 StartZ=0 EndX=5.82302 EndY=1.44654 EndZ=0
    g2: LineSegment StartX=5.82302 StartY=-1.44654 StartZ=0 EndX=8 EndY=-1.44654 EndZ=0
    g3: LineSegment StartX=8 StartY=-1.44654 StartZ=0 EndX=8 EndY=1.44654 EndZ=0
  constraints (10):
    c: Diameter(g0) = 12
    c: Coincident(g2,g3)
    c: Coincident(g3,g1)
    c: Distance(g0,g3) = 2
    c: Coincident(g1,g0)
    c: Coincident(g2,g0)
    c: Coincident(g0,g-1)
    c: Vertical(g3)
    c: Horizontal(g1)
    c: Horizontal(g2)
FEATURE [PartDesign::Pad] Pad001
  Direction = (0,-1,2e-16)
  Length = 5
  Length2 = 10
  Placement = pos=(0,0,0) rot=(1,0,0;1.5708rad)
  Profile = -> Sketch004
  ReferenceAxis = -> Sketch004 [N_Axis]
  Refine = true
  Suppressed = false
  Type = 0
FEATURE [Sketcher::SketchObject] Sketch005
  ArcFitTolerance = 1e-06
  AttachmentSupport = -> [Pad001]
  FullyConstrained = false
  MakeInternals = false
  MapMode = 5
  Placement = pos=(0,0,0) rot=(-1,0,0;1.5708rad)
  sketch-geometry (5):
    g0: ArcOfCircle CenterX=7.97057e-08 CenterY=1.58931e-06 CenterZ=0 NormalX=0 NormalY=0 NormalZ=1 AngleXU=0 Radius=5 StartAngle=1.71269 EndAngle=2.9997
    g1: LineSegment StartX=4.94975 StartY=-0.707107 StartZ=0 EndX=-0.707105 EndY=4.94975 EndZ=0
    g2: LineSegment StartX=-4.94975 StartY=0.707105 StartZ=0 EndX=0.707107 EndY=-4.94975 EndZ=0
    g3: GeomPoint [constr] X=7.97057e-08 Y=1.58931e-06 Z=0
    g4: ArcOfCircle CenterX=7.97057e-08 CenterY=1.58931e-06 CenterZ=0 NormalX=0 NormalY=0 NormalZ=1 AngleXU=0 Radius=5 StartAngle=4.85429 EndAngle=6.14129
  constraints (9):
    c: Diameter(g0) = 10
    c: Coincident(g3,g0)
    c: Coincident(g0,g1)
    c: Equal(g0,g4)
    c: Coincident(g0,g2)
    c: Coincident(g0,g4)
    c: Coincident(g1,g4)
    c: Coincident(g2,g4)
    c: Distance(g0,g1) = 3
FEATURE [PartDesign::Pad] Pad002
  BaseFeature = -> Pad001
  Direction = (0,1,2e-16)
  Length = 26
  Length2 = 10
  Placement = pos=(0,0,0) rot=(1,0,0;1.5708rad)
  Profile = -> Sketch005
  ReferenceAxis = -> Sketch005 [N_Axis]
  Refine = true
  Suppressed = false
  Type = 0
FEATURE [Sketcher::SketchObject] Sketch006
  ArcFitTolerance = 1e-06
  AttachmentSupport = -> [Pad002]
  FullyConstrained = false
  MakeInternals = false
  MapMode = 5
  Placement = pos=(0,-5,0) rot=(1,0,0;1.5708rad)
  sketch-geometry (5):
    g0: ArcOfCircle CenterX=1.75079e-07 CenterY=0 CenterZ=0 NormalX=0 NormalY=0 NormalZ=1 AngleXU=0 Radius=5 StartAngle=3.28349 EndAngle=4.57049
    g1: LineSegment StartX=-0.707107 StartY=-4.94975 StartZ=0 EndX=4.94975 EndY=0.707105 EndZ=0
    g2: LineSegment StartX=0.707107 StartY=4.94975 StartZ=0 EndX=-4.94975 EndY=-0.707107 EndZ=0
    g3: GeomPoint [constr] X=1.75079e-07 Y=0 Z=0
    g4: ArcOfCircle CenterX=1.75079e-07 CenterY=0 CenterZ=0 NormalX=0 NormalY=0 NormalZ=1 AngleXU=0 Radius=5 StartAngle=0.141897 EndAngle=1.4289
  constraints (8):
    c: Diameter(g0) = 10
    c: Coincident(g3,g0)
    c: Equal(g0,g4)
    c: Coincident(g0,g4)
    c: Coincident(g2,g4)
    c: Coincident(g1,g4)
    c: Coincident(g2,g0)
    c: Coincident(g1,g0)
FEATURE [PartDesign::Pad] Pad003
  BaseFeature = -> Pad002
  Direction = (0,-1,2e-16)
  Length = 15
  Length2 = 10
  Placement = pos=(0,0,0) rot=(1,0,0;1.5708rad)
  Profile = -> Sketch006
  ReferenceAxis = -> Sketch006 [N_Axis]
  Refine = true
  Suppressed = false
  Type = 0
FEATURE [Sketcher::SketchObject] Sketch015
  ArcFitTolerance = 1e-06
  AttachmentSupport = -> [Pad003]
  FullyConstrained = true
  MakeInternals = false
  MapMode = 5
  Placement = pos=(0,-20,0) rot=(1,0,0;1.5708rad)
  sketch-geometry (1):
    g0: Circle CenterX=0 CenterY=0 CenterZ=0 NormalX=0 NormalY=0 NormalZ=1 AngleXU=0 Radius=1.5
  constraints (2):
    c: Coincident(g0,g-1)
    c: Diameter(g0) = 3
FEATURE [Sketcher::SketchObject] Sketch016
  ArcFitTolerance = 1e-06
  AttachmentSupport = -> [Pad003]
  FullyConstrained = true
  MakeInternals = false
  MapMode = 5
  Placement = pos=(0,26,0) rot=(-1,0,0;1.5708rad)
  sketch-geometry (1):
    g0: Circle CenterX=0 CenterY=0 CenterZ=0 NormalX=0 NormalY=0 NormalZ=1 AngleXU=0 Radius=1.5
  constraints (2):
    c: Coincident(g0,g-1)
    c: Diameter(g0) = 3
FEATURE [PartDesign::Pocket] Pocket005
  BaseFeature = -> Pad003
  Direction = (0,-1,-2e-16)
  Length = 5
  Length2 = 5
  Placement = pos=(0,0,0) rot=(1,0,0;1.5708rad)
  Profile = -> Sketch016
  ReferenceAxis = -> Sketch016 [N_Axis]
  Refine = true
  Suppressed = false
  Type = 0
FEATURE [PartDesign::Pocket] Pocket006
  BaseFeature = -> Pocket005
  Direction = (0,1,-2e-16)
  Length = 5
  Length2 = 5
  Placement = pos=(0,0,0) rot=(1,0,0;1.5708rad)
  Profile = -> Sketch015
  ReferenceAxis = -> Sketch015 [N_Axis]
  Refine = true
  Suppressed = false
  Type = 0
FEATURE [PartDesign::Body] Body002  label="LowerShaft"
  AllowCompound = false
  Group = -> [Sketch004,Pad001,Sketch005,Pad002,Sketch006,Pad003,Sketch015,Sketch016,Pocket005,Pocket006]
  Origin = -> Origin003
  Placement = pos=(31,-24,-24) rot=(0,1,0;3.92699rad)
  Tip = -> Pocket006
PROVENANCE & LICENSES
A FreeCAD (.FCStd) document from a public repository crawl; recipes are the document's own serialized feature recipes (and, for linked parts, companion documents' recipes).
License: as declared in the source repository (recorded in the dataset sidecar).
